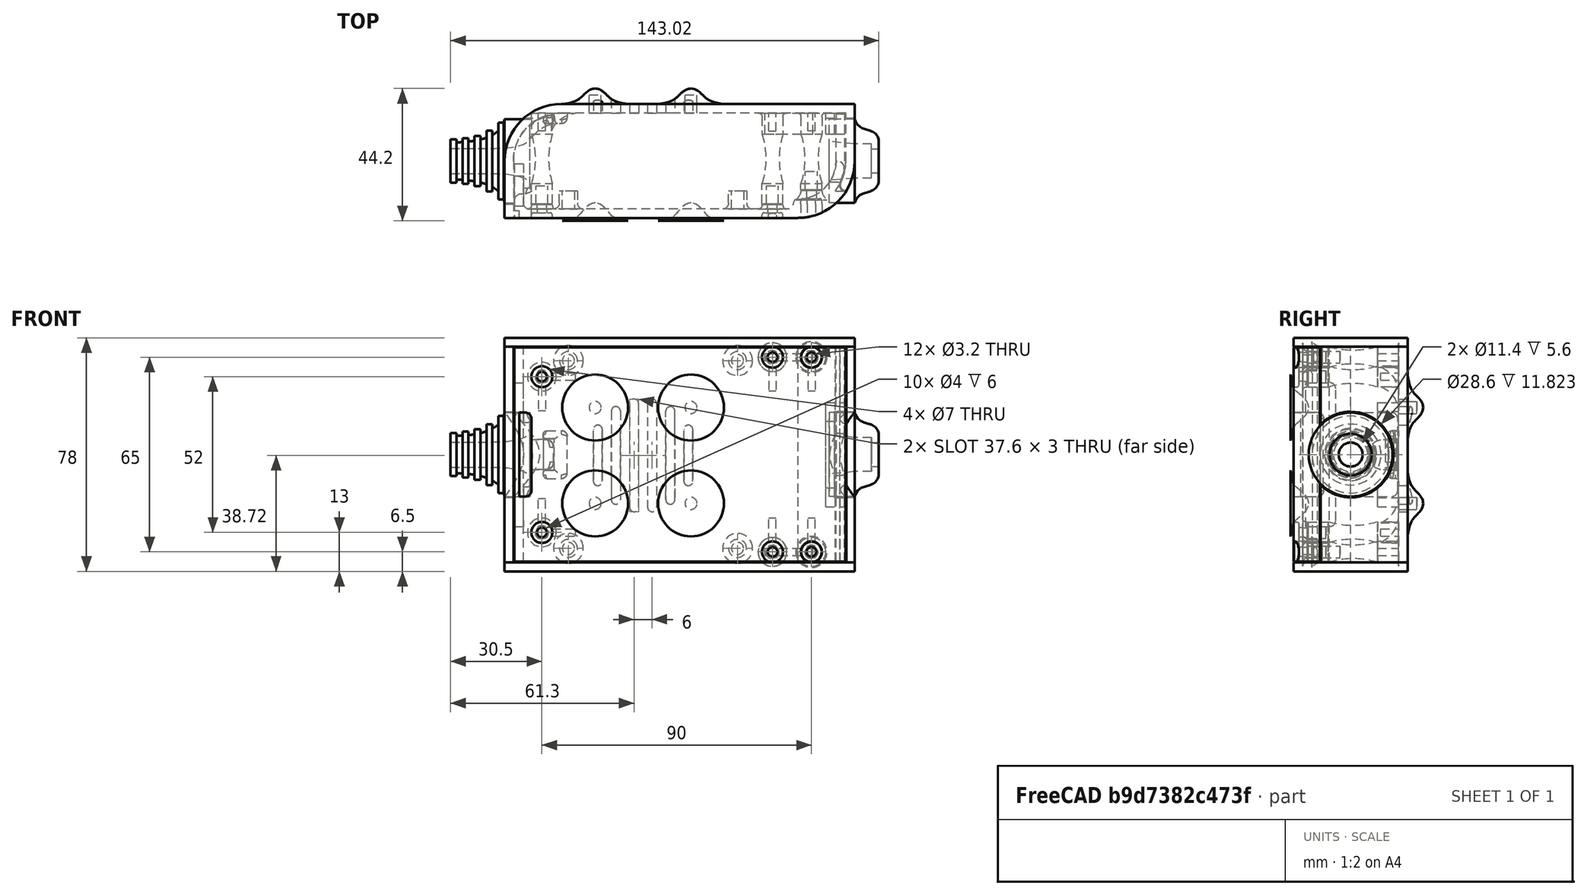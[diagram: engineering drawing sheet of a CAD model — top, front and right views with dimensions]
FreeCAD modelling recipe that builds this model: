
FCSTD DOCUMENT  (FreeCAD 0.19R0.19.2)
Label: enclosure_098
License: All rights reserved
LicenseURL: http://en.wikipedia.org/wiki/All_rights_reserved
objects: Part::Feature×72, Part::Revolution×72, Part::MultiFuse×53, Sketcher::SketchObject×30, Part::Fillet×22, Part::Cylinder×22, Part::Cut×20, Part::Extrusion×19, Part::Box×12, App::MeasureDistance×4
note: 322 computed .brp shape members not serialized (recipe doc carries the construction recipe); baked Part::Feature solids carry a one-line shape summary decoded from their .brp

FEATURE [Sketcher::SketchObject] Sketch  label="topSketch"
  FullyConstrained = true
  sketch-geometry (13):
    g0: LineSegment StartX=117 StartY=19 StartZ=0 EndX=117 EndY=38 EndZ=0
    g1: ArcOfCircle CenterX=98 CenterY=19 CenterZ=0 NormalX=0 NormalY=0 NormalZ=1 AngleXU=0 Radius=19 StartAngle=5.7297 EndAngle=6.28319
    g2: LineSegment StartX=0 StartY=3 StartZ=0 EndX=0 EndY=19 EndZ=0
    g3: LineSegment StartX=19 StartY=38 StartZ=0 EndX=117 EndY=38 EndZ=0
    g4: ArcOfCircle CenterX=19 CenterY=19 CenterZ=0 NormalX=0 NormalY=0 NormalZ=1 AngleXU=0 Radius=19 StartAngle=1.5708 EndAngle=3.14159
    g5: ArcOfCircle CenterX=19 CenterY=19 CenterZ=0 NormalX=0 NormalY=0 NormalZ=1 AngleXU=0 Radius=16 StartAngle=1.5708 EndAngle=3.14159
    g6: ArcOfCircle CenterX=98 CenterY=19 CenterZ=0 NormalX=0 NormalY=0 NormalZ=1 AngleXU=0 Radius=16 StartAngle=5.60905 EndAngle=6.28319
    g7: LineSegment StartX=114 StartY=19 StartZ=0 EndX=114 EndY=35 EndZ=0
    g8: LineSegment StartX=110.5 StartY=9.01251 StartZ=0 EndX=114.163 EndY=9.01251 EndZ=0
    g9: LineSegment StartX=114 StartY=35 StartZ=0 EndX=19 EndY=35 EndZ=0
    g10: LineSegment StartX=0 StartY=3 StartZ=0 EndX=0 EndY=0 EndZ=0
    g11: LineSegment StartX=3 StartY=0 StartZ=0 EndX=0 EndY=0 EndZ=0
    g12: LineSegment StartX=3 StartY=19 StartZ=0 EndX=3 EndY=0 EndZ=0
  constraints (33):
    c: Vertical(g0)
    c: Distance(g0) = 19
    c: Block(g0)
    c: Coincident(g1,g0)
    c: Block(g1)
    c: Vertical(g2)
    c: Block(g2)
    c: Coincident(g3,g0)
    c: Horizontal(g3)
    c: Distance(g3) = 98
    c: Coincident(g4,g3)
    c: Coincident(g4,g2)
    c: Block(g4)
    c: Coincident(g5,g4)
    c: Coincident(g6,g1)
    c: Block(g6)
    c: Block(g5)
    c: Coincident(g7,g6)
    c: Vertical(g7)
    c: Coincident(g8,g6)
    c: Coincident(g8,g1)
    c: Coincident(g9,g7)
    c: Coincident(g9,g5)
    c: Horizontal(g9)
    c: Tangent(g9,g5)
    c: Coincident(g10,g2)
    c: Distance(g10) = 3
    c: Vertical(g10)
    c: Coincident(g11,g10)
    c: Horizontal(g11)
    c: Coincident(g12,g5)
    c: Coincident(g12,g11)
    c: Vertical(g12)
FEATURE [Sketcher::SketchObject] Sketch001  label="bottomSketch"
  FullyConstrained = true
  sketch-geometry (32):
    g0: LineSegment StartX=3.3 StartY=-6.03275e-07 StartZ=0 EndX=98 EndY=-6.03275e-07 EndZ=0
    g1: ArcOfCircle CenterX=98 CenterY=19 CenterZ=0 NormalX=0 NormalY=0 NormalZ=1 AngleXU=0 Radius=19 StartAngle=4.71239 EndAngle=5.71103
    g2: LineSegment StartX=6.3 StartY=8 StartZ=0 EndX=3.3 EndY=8 EndZ=0
    g3: LineSegment StartX=3.3 StartY=8 StartZ=0 EndX=3.3 EndY=-6.03275e-07 EndZ=0
    g4: ArcOfCircle CenterX=8.3 CenterY=5 CenterZ=0 NormalX=0 NormalY=0 NormalZ=1 AngleXU=0 Radius=2 StartAngle=3.14159 EndAngle=4.71239
    g5: LineSegment StartX=6.3 StartY=8 StartZ=0 EndX=6.3 EndY=5 EndZ=0
    g6: ArcOfCircle CenterX=98 CenterY=19 CenterZ=0 NormalX=0 NormalY=0 NormalZ=1 AngleXU=0 Radius=12.7 StartAngle=4.71239 EndAngle=6.28319
    g7: LineSegment StartX=94.7 StartY=3 StartZ=0 EndX=8.3 EndY=3 EndZ=0
    g8-g12: Circle x5 (B-spline internal-alignment scaffolding for g13; pole/knot coordinates omitted)
    g13: BSplineCurve PolesCount=5 KnotsCount=3 Degree=3 IsPeriodic=0
    g14: GeomPoint X=98 Y=6.3 Z=0
    g15: GeomPoint X=96.3938 Y=4.71946 Z=0
    g16: GeomPoint X=94.7 Y=3 Z=0
    g17-g23: Circle x7 (B-spline internal-alignment scaffolding for g24; pole/knot coordinates omitted)
    g24: BSplineCurve PolesCount=7 KnotsCount=5 Degree=3 IsPeriodic=0
    g25-g29: GeomPoint x5 (B-spline internal-alignment scaffolding for g24; pole/knot coordinates omitted)
    g30: ArcOfCircle CenterX=98 CenterY=19 CenterZ=0 NormalX=0 NormalY=0 NormalZ=1 AngleXU=0 Radius=15.7 StartAngle=5.81226 EndAngle=6.28319
    g31: LineSegment StartX=110.7 StartY=19 StartZ=0 EndX=113.7 EndY=19 EndZ=0
  constraints (41):
    c: Horizontal(g0)
    c: Coincident(g1,g0)
    c: Block(g1)
    c: Horizontal(g2)
    c: Distance(g2) = 3
    c: Coincident(g3,g2)
    c: Vertical(g3)
    c: Coincident(g3,g0)
    c: Block(g4)
    c: Block(g2)
    c: Coincident(g5,g2)
    c: Coincident(g5,g4)
    c: Vertical(g5)
    c: Coincident(g6,g1)
    c: Block(g6)
    c: Coincident(g7,g4)
    c: Horizontal(g7)
    c: Block(g0)
    c: Block(g7)
    c: Block(g3)
    c: Coincident(g13,g6)
    c: Weight(g8) = 1
    c: Equal(g8, g9-g12) x4
    c: Coincident(g13,g7)
    c: InternalAlignment(g8-g12 -> g13) x5
    c: InternalAlignment(g14,g13)
    c: InternalAlignment(g15,g13)
    c: InternalAlignment(g16,g13)
    c: Block(g13)
    c: Weight(g17) = 1
    c: Equal(g17, g18-g23) x6
    c: Coincident(g24,g1)
    c: InternalAlignment(g17-g23 -> g24) x7
    c: InternalAlignment(g25-g29 -> g24) x5
    c: Block(g24)
    c: Coincident(g30,g24)
    c: Coincident(g31,g6)
    c: Coincident(g31,g30)
    c: Horizontal(g31)
    c: Block(g31)
    c: Block(g30)
FEATURE [Part::Extrusion] Extrude  label="top"
  Base = -> Sketch
  Dir = (0,0,1)
  DirMode = 2
  FaceMakerClass = Part::FaceMakerBullseye
  LengthFwd = 72
  LengthRev = 0
  Solid = true
  Symmetric = false
FEATURE [Part::Extrusion] Extrude001  label="bottom"
  Base = -> Sketch001
  Dir = (0,0,1)
  DirMode = 2
  FaceMakerClass = Part::FaceMakerBullseye
  LengthFwd = 71.4
  LengthRev = 0
  Placement = pos=(0,0,0.3) rot=(0,0,1;0rad)
  Solid = true
  Symmetric = false
FEATURE [Sketcher::SketchObject] Sketch002  label="topSketch001"
  FullyConstrained = true
  sketch-geometry (6):
    g0: LineSegment StartX=19 StartY=38 StartZ=0 EndX=117 EndY=38 EndZ=0
    g1: ArcOfCircle CenterX=19 CenterY=19 CenterZ=0 NormalX=0 NormalY=0 NormalZ=1 AngleXU=0 Radius=19 StartAngle=1.5708 EndAngle=3.14159
    g2: LineSegment StartX=117 StartY=38 StartZ=0 EndX=117 EndY=19 EndZ=0
    g3: LineSegment StartX=98 StartY=1.0161e-12 StartZ=0 EndX=5.22862e-06 EndY=1.0161e-12 EndZ=0
    g4: LineSegment StartX=5.22862e-06 StartY=19 StartZ=0 EndX=5.22862e-06 EndY=1.0161e-12 EndZ=0
    g5: ArcOfCircle CenterX=98 CenterY=19 CenterZ=0 NormalX=0 NormalY=0 NormalZ=1 AngleXU=0 Radius=19 StartAngle=4.71239 EndAngle=6.28319
  constraints (16):
    c: Horizontal(g0)
    c: Distance(g0) = 98
    c: Coincident(g1,g0)
    c: Block(g1)
    c: Coincident(g2,g0)
    c: Vertical(g2)
    c: Distance(g2) = 19
    c: Horizontal(g3)
    c: Coincident(g4,g1)
    c: Vertical(g4)
    c: Coincident(g3,g4)
    c: Block(g3)
    c: Coincident(g5,g2)
    c: Coincident(g5,g3)
    c: Block(g0)
    c: Block(g5)
FEATURE [Part::Extrusion] Extrude002  label="sideA"
  Base = -> Sketch002
  Dir = (0,0,1)
  DirMode = 2
  FaceMakerClass = Part::FaceMakerBullseye
  LengthFwd = 3
  LengthRev = 0
  Placement = pos=(0,0,-3) rot=(0,0,1;0rad)
  Solid = true
  Symmetric = false
FEATURE [Sketcher::SketchObject] Sketch003  label="topSketch002"
  FullyConstrained = true
  sketch-geometry (6):
    g0: LineSegment StartX=19 StartY=38 StartZ=0 EndX=117 EndY=38 EndZ=0
    g1: ArcOfCircle CenterX=19 CenterY=19 CenterZ=0 NormalX=0 NormalY=0 NormalZ=1 AngleXU=0 Radius=19 StartAngle=1.5708 EndAngle=3.14159
    g2: LineSegment StartX=117 StartY=38 StartZ=0 EndX=117 EndY=19 EndZ=0
    g3: LineSegment StartX=98 StartY=1.0161e-12 StartZ=0 EndX=5.22862e-06 EndY=1.0161e-12 EndZ=0
    g4: LineSegment StartX=5.22862e-06 StartY=19 StartZ=0 EndX=5.22862e-06 EndY=1.0161e-12 EndZ=0
    g5: ArcOfCircle CenterX=98 CenterY=19 CenterZ=0 NormalX=0 NormalY=0 NormalZ=1 AngleXU=0 Radius=19 StartAngle=4.71239 EndAngle=6.28319
  constraints (16):
    c: Horizontal(g0)
    c: Distance(g0) = 98
    c: Coincident(g1,g0)
    c: Block(g1)
    c: Coincident(g2,g0)
    c: Vertical(g2)
    c: Distance(g2) = 19
    c: Horizontal(g3)
    c: Coincident(g4,g1)
    c: Vertical(g4)
    c: Coincident(g3,g4)
    c: Block(g3)
    c: Coincident(g5,g2)
    c: Coincident(g5,g3)
    c: Block(g0)
    c: Block(g5)
FEATURE [Part::Extrusion] Extrude003  label="sideB"
  Base = -> Sketch003
  Dir = (0,0,1)
  DirMode = 2
  FaceMakerClass = Part::FaceMakerBullseye
  LengthFwd = 3
  LengthRev = 0
  Placement = pos=(0,0,72) rot=(0,0,1;0rad)
  Solid = true
  Symmetric = false
FEATURE [Sketcher::SketchObject] Sketch004
  FullyConstrained = true
  MapMode = 3
  Placement = pos=(0,0,0) rot=(1,0,0;1.5708rad)
  Support = -> [Extrude]
  sketch-geometry (8):
    g0: Circle CenterX=80.351 CenterY=-67.6202 CenterZ=0 NormalX=0 NormalY=0 NormalZ=1 AngleXU=0 Radius=2
    g1: Circle CenterX=80.351 CenterY=-67.6202 CenterZ=0 NormalX=0 NormalY=0 NormalZ=1 AngleXU=0 Radius=3
    g2: Circle CenterX=80.351 CenterY=-4.92017 CenterZ=0 NormalX=0 NormalY=0 NormalZ=1 AngleXU=0 Radius=2
    g3: Circle CenterX=80.351 CenterY=-4.92017 CenterZ=0 NormalX=0 NormalY=0 NormalZ=1 AngleXU=0 Radius=3
    g4: Circle CenterX=23.851 CenterY=-4.92017 CenterZ=0 NormalX=0 NormalY=0 NormalZ=1 AngleXU=0 Radius=2
    g5: Circle CenterX=23.851 CenterY=-4.92017 CenterZ=0 NormalX=0 NormalY=0 NormalZ=1 AngleXU=0 Radius=3
    g6: Circle CenterX=23.851 CenterY=-67.6202 CenterZ=0 NormalX=0 NormalY=0 NormalZ=1 AngleXU=0 Radius=2
    g7: Circle CenterX=23.851 CenterY=-67.6202 CenterZ=0 NormalX=0 NormalY=0 NormalZ=1 AngleXU=0 Radius=3
  constraints (8):
    c: Block(g3)
    c: Block(g2)
    c: Block(g1)
    c: Block(g0)
    c: Block(g6)
    c: Block(g7)
    c: Block(g4)
    c: Block(g5)
FEATURE [Part::Extrusion] Extrude004
  Base = -> Sketch004
  Dir = (0,-1,2e-16)
  DirMode = 2
  FaceMakerClass = Part::FaceMakerBullseye
  LengthFwd = 6
  LengthRev = 0
  Placement = pos=(0,9,0) rot=(0,0,1;0rad)
  Solid = true
  Symmetric = false
FEATURE [Sketcher::SketchObject] Sketch005
  FullyConstrained = true
  MapMode = 3
  Placement = pos=(0,0,0) rot=(1,0,0;1.5708rad)
  Support = -> [Extrude]
  sketch-geometry (8):
    g0: Circle CenterX=80.351 CenterY=-67.6202 CenterZ=0 NormalX=0 NormalY=0 NormalZ=1 AngleXU=0 Radius=3
    g1: Circle CenterX=80.351 CenterY=-4.92017 CenterZ=0 NormalX=0 NormalY=0 NormalZ=1 AngleXU=0 Radius=3
    g2: Circle CenterX=23.851 CenterY=-4.92017 CenterZ=0 NormalX=0 NormalY=0 NormalZ=1 AngleXU=0 Radius=3
    g3: Circle CenterX=23.851 CenterY=-67.6202 CenterZ=0 NormalX=0 NormalY=0 NormalZ=1 AngleXU=0 Radius=3
    g4: Circle CenterX=23.851 CenterY=-67.6202 CenterZ=0 NormalX=0 NormalY=0 NormalZ=1 AngleXU=0 Radius=5
    g5: Circle CenterX=80.351 CenterY=-67.6202 CenterZ=0 NormalX=0 NormalY=0 NormalZ=1 AngleXU=0 Radius=5
    g6: Circle CenterX=23.851 CenterY=-4.92017 CenterZ=0 NormalX=0 NormalY=0 NormalZ=1 AngleXU=0 Radius=5
    g7: Circle CenterX=80.351 CenterY=-4.92017 CenterZ=0 NormalX=0 NormalY=0 NormalZ=1 AngleXU=0 Radius=5
  constraints (8):
    c: Block(g1)
    c: Block(g0)
    c: Block(g3)
    c: Block(g2)
    c: Block(g5)
    c: Block(g4)
    c: Block(g6)
    c: Block(g7)
FEATURE [Part::Extrusion] Extrude005
  Base = -> Sketch005
  Dir = (0,-1,2e-16)
  DirMode = 2
  FaceMakerClass = Part::FaceMakerBullseye
  LengthFwd = 2
  LengthRev = 0
  Solid = true
  Symmetric = false
FEATURE [Sketcher::SketchObject] Sketch006
  FullyConstrained = true
  MapMode = 3
  Placement = pos=(0,0,0) rot=(1,0,0;1.5708rad)
  sketch-geometry (8):
    g0: Circle CenterX=80.351 CenterY=-67.6202 CenterZ=0 NormalX=0 NormalY=0 NormalZ=1 AngleXU=0 Radius=3
    g1: Circle CenterX=80.351 CenterY=-4.92017 CenterZ=0 NormalX=0 NormalY=0 NormalZ=1 AngleXU=0 Radius=3
    g2: Circle CenterX=23.851 CenterY=-4.92017 CenterZ=0 NormalX=0 NormalY=0 NormalZ=1 AngleXU=0 Radius=3
    g3: Circle CenterX=23.851 CenterY=-67.6202 CenterZ=0 NormalX=0 NormalY=0 NormalZ=1 AngleXU=0 Radius=3
    g4: Circle CenterX=23.851 CenterY=-67.6202 CenterZ=0 NormalX=0 NormalY=0 NormalZ=1 AngleXU=0 Radius=5
    g5: Circle CenterX=80.351 CenterY=-67.6202 CenterZ=0 NormalX=0 NormalY=0 NormalZ=1 AngleXU=0 Radius=5
    g6: Circle CenterX=23.851 CenterY=-4.92017 CenterZ=0 NormalX=0 NormalY=0 NormalZ=1 AngleXU=0 Radius=5
    g7: Circle CenterX=80.351 CenterY=-4.92017 CenterZ=0 NormalX=0 NormalY=0 NormalZ=1 AngleXU=0 Radius=5
  constraints (8):
    c: Block(g1)
    c: Block(g0)
    c: Block(g3)
    c: Block(g2)
    c: Block(g5)
    c: Block(g4)
    c: Block(g6)
    c: Block(g7)
FEATURE [Part::Extrusion] Extrude007
  Base = -> Sketch006
  Dir = (0,-1,2e-16)
  DirMode = 2
  FaceMakerClass = Part::FaceMakerBullseye
  LengthFwd = 2
  LengthRev = 0
  Solid = true
  Symmetric = false
FEATURE [Part::Fillet] Fillet
  Base = -> Extrude007
  Edges = 4 edges r=1.99: [Edge6,Edge12,Edge18,Edge24]
FEATURE [Part::Cut] Cut
  Base = -> Extrude005
  Placement = pos=(0,5,0) rot=(0,0,1;0rad)
  Tool = -> Fillet
FEATURE [Part::MultiFuse] Fusion  label="pCBScrews"
  Placement = pos=(-2.5,0,72.3) rot=(0,0,1;0rad)
  Shapes = -> [Extrude004,Cut]
FEATURE [App::MeasureDistance] Distance  label="Distance: 0.69 mm"
  Distance = 0.685967
  P1 = (24.0138,2.9647,0.3)
  P2 = (23.8901,3,-0.373787)
FEATURE [App::MeasureDistance] Distance001  label="Distance: 0.53 mm"
  Distance = 0.533607
  P1 = (80.2939,3,72.2334)
  P2 = (80.281,2.99661,71.7)
FEATURE [Part::Fillet] Fillet001
  Base = -> Extrude001
  Edges = 1 edges r=2.4: [Edge17]
FEATURE [Part::Fillet] Fillet002  label="bottom001"
  Base = -> Fillet001
  Edges = 1 edges r=2.4: [Edge36]
FEATURE [Part::Fillet] Fillet003  label="top001"
  Base = -> Extrude
  Edges = 1 edges r=2: [Edge1]
FEATURE [Sketcher::SketchObject] Sketch007
  FullyConstrained = true
  sketch-geometry (16):
    g0: LineSegment StartX=4 StartY=0 StartZ=0 EndX=4 EndY=2.4 EndZ=0
    g1: LineSegment StartX=4 StartY=2.4 StartZ=0 EndX=7 EndY=2.4 EndZ=0
    g2: LineSegment StartX=4 StartY=0 StartZ=0 EndX=5.7 EndY=0 EndZ=0
    g3: LineSegment StartX=5.7 StartY=0 StartZ=0 EndX=5.7 EndY=-5.6 EndZ=0
    g4-g8: Circle x5 (B-spline internal-alignment scaffolding for g9; pole/knot coordinates omitted)
    g9: BSplineCurve PolesCount=5 KnotsCount=3 Degree=3 IsPeriodic=0
    g10: GeomPoint X=7 Y=2.4 Z=0
    g11: GeomPoint X=10.4582 Y=-1.55472 Z=0
    g12: GeomPoint X=14 Y=-5.6 Z=0
    g13: LineSegment StartX=14 StartY=-5.6 StartZ=0 EndX=14 EndY=-14.1 EndZ=0
    g14: LineSegment StartX=14 StartY=-14.1 StartZ=0 EndX=6.5 EndY=-14.1 EndZ=0
    g15: LineSegment StartX=5.7 StartY=-5.6 StartZ=0 EndX=6.5 EndY=-14.1 EndZ=0
  constraints (28):
    c: Distance(g0) = 2.4
    c: Vertical(g0)
    c: Block(g0)
    c: Coincident(g1,g0)
    c: Horizontal(g1)
    c: Distance(g1) = 3
    c: Coincident(g2,g0)
    c: Horizontal(g2)
    c: Distance(g2) = 1.7
    c: Coincident(g3,g2)
    c: Vertical(g3)
    c: Distance(g3) = 5.6
    c: Coincident(g9,g1)
    c: Weight(g4) = 1
    c: Equal(g4, g5-g8) x4
    c: InternalAlignment(g4-g8 -> g9) x5
    c: InternalAlignment(g10,g9)
    c: InternalAlignment(g11,g9)
    c: InternalAlignment(g12,g9)
    c: Block(g9)
    c: Coincident(g13,g9)
    c: Vertical(g13)
    c: Distance(g13) = 8.5
    c: Coincident(g14,g13)
    c: Horizontal(g14)
    c: Distance(g14) = 7.5
    c: Coincident(g15,g3)
    c: Coincident(g15,g14)
FEATURE [Part::Feature] Face
  shape: bbox 10 x 16.5 x 2e-07 mm, 1 faces, 0 solids (baked)
FEATURE [Part::Revolution] Revolve  label="plugHousing"
  Angle = 360
  Axis = (0,1,0)
  Base = (0,0,0)
  FaceMakerClass = Part::FaceMakerBullseye
  Placement = pos=(0,0,36.15) rot=(0,0,1;0rad)
  Solid = false
  Source = -> Face
  Symmetric = false
FEATURE [Part::Feature] Face001
  shape: bbox 10 x 16.5 x 2e-07 mm, 1 faces, 0 solids (baked)
FEATURE [Part::Revolution] Revolve001  label="plugHousing001"
  Angle = 360
  Axis = (0,1,0)
  Base = (0,0,0)
  FaceMakerClass = Part::FaceMakerBullseye
  Placement = pos=(0,0,36.15) rot=(0,0,1;0rad)
  Solid = false
  Source = -> Face001
  Symmetric = false
FEATURE [Part::MultiFuse] Fusion001  label="plugHousing002"
  Placement = pos=(0,0,0) rot=(0,0,1;1.5708rad)
  Shapes = -> [Revolve001,Revolve]
FEATURE [Part::Feature] Face002
  shape: bbox 10 x 16.5 x 2e-07 mm, 1 faces, 0 solids (baked)
FEATURE [Part::Revolution] Revolve003  label="plugHousing005"
  Angle = 360
  Axis = (0,1,0)
  Base = (0,0,0)
  FaceMakerClass = Part::FaceMakerBullseye
  Placement = pos=(0,0,36.15) rot=(0,0,1;0rad)
  Solid = false
  Source = -> Face002
  Symmetric = false
FEATURE [Part::Feature] Face003
  shape: bbox 10 x 16.5 x 2e-07 mm, 1 faces, 0 solids (baked)
FEATURE [Part::Revolution] Revolve002  label="plugHousing003"
  Angle = 360
  Axis = (0,1,0)
  Base = (0,0,0)
  FaceMakerClass = Part::FaceMakerBullseye
  Placement = pos=(0,0,36.15) rot=(0,0,1;0rad)
  Solid = false
  Source = -> Face003
  Symmetric = false
FEATURE [Part::MultiFuse] Fusion002  label="plugHousing004"
  Placement = pos=(0,0,0) rot=(0,0,1;1.5708rad)
  Shapes = -> [Revolve002,Revolve003]
FEATURE [Part::MultiFuse] Fusion003  label="plugHousing006"
  Placement = pos=(0,19,0) rot=(0,0,1;3.14159rad)
  Shapes = -> [Fusion002,Fusion001]
FEATURE [Part::Feature] Face004
  shape: bbox 10 x 16.5 x 2e-07 mm, 1 faces, 0 solids (baked)
FEATURE [Part::Revolution] Revolve006  label="plugHousing010"
  Angle = 360
  Axis = (0,1,0)
  Base = (0,0,0)
  FaceMakerClass = Part::FaceMakerBullseye
  Placement = pos=(0,0,36.15) rot=(0,0,1;0rad)
  Solid = false
  Source = -> Face004
  Symmetric = false
FEATURE [Part::Feature] Face005
  shape: bbox 10 x 16.5 x 2e-07 mm, 1 faces, 0 solids (baked)
FEATURE [Part::Revolution] Revolve007  label="plugHousing011"
  Angle = 360
  Axis = (0,1,0)
  Base = (0,0,0)
  FaceMakerClass = Part::FaceMakerBullseye
  Placement = pos=(0,0,36.15) rot=(0,0,1;0rad)
  Solid = false
  Source = -> Face005
  Symmetric = false
FEATURE [Part::Feature] Face006
  shape: bbox 10 x 16.5 x 2e-07 mm, 1 faces, 0 solids (baked)
FEATURE [Part::Revolution] Revolve004  label="plugHousing007"
  Angle = 360
  Axis = (0,1,0)
  Base = (0,0,0)
  FaceMakerClass = Part::FaceMakerBullseye
  Placement = pos=(0,0,36.15) rot=(0,0,1;0rad)
  Solid = false
  Source = -> Face006
  Symmetric = false
FEATURE [Part::MultiFuse] Fusion004  label="plugHousing009"
  Placement = pos=(0,0,0) rot=(0,0,1;1.5708rad)
  Shapes = -> [Revolve004,Revolve007]
FEATURE [Part::Feature] Face007
  shape: bbox 10 x 16.5 x 2e-07 mm, 1 faces, 0 solids (baked)
FEATURE [Part::Revolution] Revolve005  label="plugHousing008"
  Angle = 360
  Axis = (0,1,0)
  Base = (0,0,0)
  FaceMakerClass = Part::FaceMakerBullseye
  Placement = pos=(0,0,36.15) rot=(0,0,1;0rad)
  Solid = false
  Source = -> Face007
  Symmetric = false
FEATURE [Part::MultiFuse] Fusion005  label="plugHousing012"
  Placement = pos=(0,0,0) rot=(0,0,1;1.5708rad)
  Shapes = -> [Revolve006,Revolve005]
FEATURE [Part::MultiFuse] Fusion006  label="plugHousing013"
  Placement = pos=(0,19,0) rot=(0,0,1;3.14159rad)
  Shapes = -> [Fusion005,Fusion004]
FEATURE [Part::MultiFuse] Fusion007  label="plugHousing014"
  Placement = pos=(122.621,0,-0.15) rot=(0,0,1;0rad)
  Shapes = -> [Fusion003,Fusion006]
FEATURE [Part::Cylinder] Cylinder002
  Angle = 360
  AttacherType = Attacher::AttachEngine3D
  Height = 20
  Placement = pos=(0,0,36.15) rot=(0,0,1;0rad)
  Radius = 4
FEATURE [Part::Cylinder] Cylinder003
  Angle = 360
  AttacherType = Attacher::AttachEngine3D
  Height = 10
  Placement = pos=(0,0,36.15) rot=(0,0,1;0rad)
  Radius = 4
FEATURE [Part::MultiFuse] Fusion009  label="removeToCreateHoleForPlugHousing"
  Placement = pos=(70,19,36.15) rot=(0,1,0;1.5708rad)
  Shapes = -> [Cylinder002,Cylinder003]
FEATURE [Part::Cylinder] Cylinder004
  Angle = 360
  AttacherType = Attacher::AttachEngine3D
  Height = 20
  Placement = pos=(0,0,36.15) rot=(0,0,1;0rad)
  Radius = 4
FEATURE [Part::Cylinder] Cylinder005
  Angle = 360
  AttacherType = Attacher::AttachEngine3D
  Height = 10
  Placement = pos=(0,0,36.15) rot=(0,0,1;0rad)
  Radius = 4
FEATURE [Part::MultiFuse] Fusion010  label="removeToCreateHoleForPlugHousing001"
  Placement = pos=(70,19,36.15) rot=(0,1,0;1.5708rad)
  Shapes = -> [Cylinder004,Cylinder005]
FEATURE [Part::Cut] Cut001
  Base = -> Fillet003
  Tool = -> Fusion010
FEATURE [Part::Cut] Cut002  label="Bottom"
  Base = -> Fillet002
  Tool = -> Fusion009
FEATURE [Part::Feature] Face008
  shape: bbox 10 x 16.5 x 2e-07 mm, 1 faces, 0 solids (baked)
FEATURE [Part::Revolution] Revolve011  label="plugHousing021"
  Angle = 360
  Axis = (0,1,0)
  Base = (0,0,0)
  FaceMakerClass = Part::FaceMakerBullseye
  Placement = pos=(0,0,36.15) rot=(0,0,1;0rad)
  Solid = false
  Source = -> Face008
  Symmetric = false
FEATURE [Part::Feature] Face009
  shape: bbox 10 x 16.5 x 2e-07 mm, 1 faces, 0 solids (baked)
FEATURE [Part::Revolution] Revolve012  label="plugHousing022"
  Angle = 360
  Axis = (0,1,0)
  Base = (0,0,0)
  FaceMakerClass = Part::FaceMakerBullseye
  Placement = pos=(0,0,36.15) rot=(0,0,1;0rad)
  Solid = false
  Source = -> Face009
  Symmetric = false
FEATURE [Part::Feature] Face010 .. Face013  x4 (patterned run collapsed; names and placements below)
  shape: bbox 10 x 16.5 x 2e-07 mm, 1 faces, 0 solids (baked)
FEATURE [Part::Revolution] Revolve015  label="plugHousing027"
  Angle = 360
  Axis = (0,1,0)
  Base = (0,0,0)
  FaceMakerClass = Part::FaceMakerBullseye
  Placement = pos=(0,0,36.15) rot=(0,0,1;0rad)
  Solid = false
  Source = -> Face013
  Symmetric = false
FEATURE [Part::Feature] Face014
  shape: bbox 10 x 16.5 x 2e-07 mm, 1 faces, 0 solids (baked)
FEATURE [Part::Feature] Face015
  shape: bbox 10 x 16.5 x 2e-07 mm, 1 faces, 0 solids (baked)
FEATURE [Part::Feature] Face016
  shape: bbox 10 x 16.5 x 2e-07 mm, 1 faces, 0 solids (baked)
FEATURE [Part::Revolution] Revolve019  label="plugHousing033"
  Angle = 360
  Axis = (0,1,0)
  Base = (0,0,0)
  FaceMakerClass = Part::FaceMakerBullseye
  Placement = pos=(0,0,36.15) rot=(0,0,1;0rad)
  Solid = false
  Source = -> Face016
  Symmetric = false
FEATURE [Part::Feature] Face017
  shape: bbox 10 x 16.5 x 2e-07 mm, 1 faces, 0 solids (baked)
FEATURE [Part::Revolution] Revolve020  label="plugHousing034"
  Angle = 360
  Axis = (0,1,0)
  Base = (0,0,0)
  FaceMakerClass = Part::FaceMakerBullseye
  Placement = pos=(0,0,36.15) rot=(0,0,1;0rad)
  Solid = false
  Source = -> Face017
  Symmetric = false
FEATURE [Part::Feature] Face018
  shape: bbox 10 x 16.5 x 2e-07 mm, 1 faces, 0 solids (baked)
FEATURE [Part::Revolution] Revolve016  label="plugHousing030"
  Angle = 360
  Axis = (0,1,0)
  Base = (0,0,0)
  FaceMakerClass = Part::FaceMakerBullseye
  Placement = pos=(0,0,36.15) rot=(0,0,1;0rad)
  Solid = false
  Source = -> Face018
  Symmetric = false
FEATURE [Part::MultiFuse] Fusion020  label="plugHousing038"
  Placement = pos=(0,0,0) rot=(0,0,1;1.5708rad)
  Shapes = -> [Revolve016,Revolve020]
FEATURE [Part::Feature] Face019
  shape: bbox 10 x 16.5 x 2e-07 mm, 1 faces, 0 solids (baked)
FEATURE [Part::Feature] Face020
  shape: bbox 10 x 16.5 x 2e-07 mm, 1 faces, 0 solids (baked)
FEATURE [Part::Revolution] Revolve017  label="plugHousing031"
  Angle = 360
  Axis = (0,1,0)
  Base = (0,0,0)
  FaceMakerClass = Part::FaceMakerBullseye
  Placement = pos=(0,0,36.15) rot=(0,0,1;0rad)
  Solid = false
  Source = -> Face020
  Symmetric = false
FEATURE [Part::MultiFuse] Fusion021  label="plugHousing039"
  Placement = pos=(0,0,0) rot=(0,0,1;1.5708rad)
  Shapes = -> [Revolve019,Revolve017]
FEATURE [Part::MultiFuse] Fusion023  label="plugHousing041"
  Placement = pos=(0,19,0) rot=(0,0,1;3.14159rad)
  Shapes = -> [Fusion021,Fusion020]
FEATURE [Part::Revolution] Revolve022  label="plugHousing043"
  Angle = 360
  Axis = (0,1,0)
  Base = (0,0,0)
  FaceMakerClass = Part::FaceMakerBullseye
  Placement = pos=(0,0,36.15) rot=(0,0,1;0rad)
  Solid = false
  Source = -> Face019
  Symmetric = false
FEATURE [Part::Feature] Face021
  shape: bbox 10 x 16.5 x 2e-07 mm, 1 faces, 0 solids (baked)
FEATURE [Part::Revolution] Revolve023  label="plugHousing044"
  Angle = 360
  Axis = (0,1,0)
  Base = (0,0,0)
  FaceMakerClass = Part::FaceMakerBullseye
  Placement = pos=(0,0,36.15) rot=(0,0,1;0rad)
  Solid = false
  Source = -> Face021
  Symmetric = false
FEATURE [Part::Feature] Face022
  shape: bbox 10 x 16.5 x 2e-07 mm, 1 faces, 0 solids (baked)
FEATURE [Part::Revolution] Revolve018  label="plugHousing032"
  Angle = 360
  Axis = (0,1,0)
  Base = (0,0,0)
  FaceMakerClass = Part::FaceMakerBullseye
  Placement = pos=(0,0,36.15) rot=(0,0,1;0rad)
  Solid = false
  Source = -> Face022
  Symmetric = false
FEATURE [Part::MultiFuse] Fusion022  label="plugHousing040"
  Placement = pos=(0,0,0) rot=(0,0,1;1.5708rad)
  Shapes = -> [Revolve018,Revolve023]
FEATURE [Part::Feature] Face023
  shape: bbox 10 x 16.5 x 2e-07 mm, 1 faces, 0 solids (baked)
FEATURE [Part::Revolution] Revolve021  label="plugHousing035"
  Angle = 360
  Axis = (0,1,0)
  Base = (0,0,0)
  FaceMakerClass = Part::FaceMakerBullseye
  Placement = pos=(0,0,36.15) rot=(0,0,1;0rad)
  Solid = false
  Source = -> Face023
  Symmetric = false
FEATURE [Part::MultiFuse] Fusion018  label="plugHousing036"
  Placement = pos=(0,0,0) rot=(0,0,1;1.5708rad)
  Shapes = -> [Revolve022,Revolve021]
FEATURE [Part::MultiFuse] Fusion019  label="plugHousing037"
  Placement = pos=(0,19,0) rot=(0,0,1;3.14159rad)
  Shapes = -> [Fusion018,Fusion022]
FEATURE [Part::MultiFuse] Fusion024  label="plugHousing042"
  Placement = pos=(122.621,0,-0.15) rot=(0,0,1;0rad)
  Shapes = -> [Fusion023,Fusion019]
FEATURE [Part::Cylinder] Cylinder006
  Angle = 360
  AttacherType = Attacher::AttachEngine3D
  Height = 20
  Placement = pos=(0,0,36.15) rot=(0,0,1;0rad)
  Radius = 14.3
FEATURE [Part::Cylinder] Cylinder007
  Angle = 360
  AttacherType = Attacher::AttachEngine3D
  Height = 10
  Placement = pos=(0,0,36.15) rot=(0,0,1;0rad)
  Radius = 4
FEATURE [Part::MultiFuse] Fusion026  label="removeToCreteHoleForPlugHousing"
  Placement = pos=(70,19,36) rot=(0,1,0;1.5708rad)
  Shapes = -> [Cylinder006,Cylinder007]
FEATURE [Part::Box] Box001  label="Cube001"
  AttacherType = Attacher::AttachEngine3D
  Height = 28
  Length = 3
  Placement = pos=(110.7,19,22) rot=(0,0,1;0rad)
  Width = 15.7
FEATURE [Part::Cut] Cut003  label="top002"
  Base = -> Cut001
  Tool = -> Fusion007
FEATURE [Part::Revolution] Revolve008  label="plugHousing015"
  Angle = 360
  Axis = (0,1,0)
  Base = (0,0,0)
  FaceMakerClass = Part::FaceMakerBullseye
  Placement = pos=(0,0,36.15) rot=(0,0,1;0rad)
  Solid = false
  Source = -> Face010
  Symmetric = false
FEATURE [Part::MultiFuse] Fusion013  label="plugHousing020"
  Placement = pos=(0,0,0) rot=(0,0,1;1.5708rad)
  Shapes = -> [Revolve008,Revolve012]
FEATURE [Part::Cut] Cut004  label="top003"
  Base = -> Cut003
  Placement = pos=(1,0,0) rot=(0,0,1;0rad)
  Tool = -> Fusion026
FEATURE [Part::Cylinder] Cylinder008
  Angle = 360
  AttacherType = Attacher::AttachEngine3D
  Height = 20
  Placement = pos=(0,0,36.15) rot=(0,0,1;0rad)
  Radius = 10.3
FEATURE [Part::Cylinder] Cylinder009
  Angle = 360
  AttacherType = Attacher::AttachEngine3D
  Height = 10
  Placement = pos=(0,0,36.15) rot=(0,0,1;0rad)
  Radius = 4
FEATURE [Part::MultiFuse] Fusion027  label="removeToCreteHoleForPlugHousing001"
  Placement = pos=(70,19,36) rot=(0,1,0;1.5708rad)
  Shapes = -> [Cylinder008,Cylinder009]
FEATURE [Part::Cut] Cut005  label="plugHousingTab"
  Base = -> Box001
  Tool = -> Fusion027
FEATURE [Part::MultiFuse] Fusion028  label="plugHousing045"
  Shapes = -> [Fusion024,Cut005]
FEATURE [Part::Box] Box002  label="Cube002"
  AttacherType = Attacher::AttachEngine3D
  Height = 28.8
  Length = 3
  Placement = pos=(107.3,28,21.6) rot=(0,0,1;0rad)
  Width = 7
FEATURE [Part::Box] Box003  label="Cube003"
  AttacherType = Attacher::AttachEngine3D
  Height = 3
  Length = 6.4
  Placement = pos=(107.3,28,18.6) rot=(0,0,1;0rad)
  Width = 7
FEATURE [Part::Box] Box004  label="Cube004"
  AttacherType = Attacher::AttachEngine3D
  Height = 3
  Length = 6.4
  Placement = pos=(107.3,28,50.4) rot=(0,0,1;0rad)
  Width = 7
FEATURE [Part::MultiFuse] Fusion029  label="plugHousingBracketHolder"
  Shapes = -> [Box004,Box002,Box003]
FEATURE [Part::Cylinder] Cylinder010
  Angle = 360
  AttacherType = Attacher::AttachEngine3D
  Height = 20
  Placement = pos=(0,0,36.15) rot=(0,0,1;0rad)
  Radius = 14.3
FEATURE [Part::Cylinder] Cylinder011
  Angle = 360
  AttacherType = Attacher::AttachEngine3D
  Height = 10
  Placement = pos=(0,0,36.15) rot=(0,0,1;0rad)
  Radius = 4
FEATURE [Part::MultiFuse] Fusion030  label="removeToCreteHoleForPlugHousing002"
  Placement = pos=(70,19,36) rot=(0,1,0;1.5708rad)
  Shapes = -> [Cylinder010,Cylinder011]
FEATURE [Part::Cut] Cut006  label="plugHousingBracketHolder001"
  Base = -> Fusion029
  Tool = -> Fusion030
FEATURE [Part::Cylinder] Cylinder012
  Angle = 360
  AttacherType = Attacher::AttachEngine3D
  Height = 20
  Placement = pos=(0,0,36.15) rot=(0,0,1;0rad)
  Radius = 7
FEATURE [Part::Cylinder] Cylinder013
  Angle = 360
  AttacherType = Attacher::AttachEngine3D
  Height = 10
  Placement = pos=(0,0,36.15) rot=(0,0,1;0rad)
  Radius = 4
FEATURE [Part::MultiFuse] Fusion032  label="removeToCreteHoleForPlugHousing003"
  Placement = pos=(70,19,36) rot=(0,1,0;1.5708rad)
  Shapes = -> [Cylinder012,Cylinder013]
FEATURE [Part::Cut] Cut007  label="bottom002"
  Base = -> Cut002
  Tool = -> Fusion032
FEATURE [Sketcher::SketchObject] Sketch008
  FullyConstrained = true
  sketch-geometry (54):
    g0: LineSegment StartX=-4.2 StartY=0 StartZ=0 EndX=-6.2 EndY=0 EndZ=0
    g1: LineSegment StartX=-14 StartY=-18 StartZ=0 EndX=-14 EndY=-26.5 EndZ=0
    g2: LineSegment StartX=-4.2 StartY=0 StartZ=0 EndX=-4.2 EndY=-13.4877 EndZ=0
    g3: Circle CenterX=-4.2 CenterY=-13.4877 CenterZ=0 NormalX=0 NormalY=0 NormalZ=1 AngleXU=0 Radius=1
    g4: Circle CenterX=-4.2 CenterY=-26.5 CenterZ=0 NormalX=0 NormalY=0 NormalZ=1 AngleXU=0 Radius=1
    g5: Circle CenterX=-8.2 CenterY=-26.5 CenterZ=0 NormalX=0 NormalY=0 NormalZ=1 AngleXU=0 Radius=1
    g6: BSplineCurve PolesCount=3 KnotsCount=2 Degree=2 IsPeriodic=0
    g7: GeomPoint X=-4.2 Y=-13.4877 Z=0
    g8: GeomPoint X=-8.2 Y=-26.5 Z=0
    g9: LineSegment StartX=-14 StartY=-26.5 StartZ=0 EndX=-8.2 EndY=-26.5 EndZ=0
    g10: LineSegment StartX=-10.15 StartY=-12 StartZ=0 EndX=-10.15 EndY=-14 EndZ=0
    g11: LineSegment StartX=-12.8401 StartY=-16 StartZ=0 EndX=-10.1571 EndY=-16 EndZ=0
    g12: LineSegment StartX=-10.15 StartY=-14 StartZ=0 EndX=-8.70761 EndY=-14 EndZ=0
    g13: LineSegment StartX=-12.8401 StartY=-16 StartZ=0 EndX=-12.8401 EndY=-17.6958 EndZ=0
    g14: LineSegment StartX=-10.15 StartY=-12 StartZ=0 EndX=-7.79258 EndY=-12 EndZ=0
    g15: Circle CenterX=-6.2215 CenterY=-2 CenterZ=0 NormalX=0 NormalY=0 NormalZ=1 AngleXU=0 Radius=1
    g16: Circle CenterX=-6.22762 CenterY=-2.58724 CenterZ=0 NormalX=0 NormalY=0 NormalZ=1 AngleXU=0 Radius=1
    g17: Circle CenterX=-6.32538 CenterY=-4 CenterZ=0 NormalX=0 NormalY=0 NormalZ=1 AngleXU=0 Radius=1
    g18: BSplineCurve PolesCount=3 KnotsCount=2 Degree=2 IsPeriodic=0
    g19: GeomPoint X=-6.2215 Y=-2 Z=0
    g20: GeomPoint X=-6.32538 Y=-4 Z=0
    g21: Circle CenterX=-6.48644 CenterY=-5.99526 CenterZ=0 NormalX=0 NormalY=0 NormalZ=1 AngleXU=0 Radius=1
    g22: Circle CenterX=-6.58486 CenterY=-6.99526 CenterZ=0 NormalX=0 NormalY=0 NormalZ=1 AngleXU=0 Radius=1
    g23: Circle CenterX=-6.77343 CenterY=-8 CenterZ=0 NormalX=0 NormalY=0 NormalZ=1 AngleXU=0 Radius=1
    g24: BSplineCurve PolesCount=3 KnotsCount=2 Degree=2 IsPeriodic=0
    g25: GeomPoint X=-6.48644 Y=-5.99526 Z=0
    g26: GeomPoint X=-6.77343 Y=-8 Z=0
    g27: Circle CenterX=-7.19003 CenterY=-10 CenterZ=0 NormalX=0 NormalY=0 NormalZ=1 AngleXU=0 Radius=1
    g28: Circle CenterX=-7.44407 CenterY=-11.0915 CenterZ=0 NormalX=0 NormalY=0 NormalZ=1 AngleXU=0 Radius=1
    g29: Circle CenterX=-7.79258 CenterY=-12 CenterZ=0 NormalX=0 NormalY=0 NormalZ=1 AngleXU=0 Radius=1
    g30: BSplineCurve PolesCount=3 KnotsCount=2 Degree=2 IsPeriodic=0
    g31: GeomPoint X=-7.19003 Y=-10 Z=0
    g32: GeomPoint X=-7.79258 Y=-12 Z=0
    g33: Circle CenterX=-8.70761 CenterY=-14 CenterZ=0 NormalX=0 NormalY=0 NormalZ=1 AngleXU=0 Radius=1
    g34: Circle CenterX=-9.33087 CenterY=-15.1837 CenterZ=0 NormalX=0 NormalY=0 NormalZ=1 AngleXU=0 Radius=1
    g35: Circle CenterX=-10.1571 CenterY=-16 CenterZ=0 NormalX=0 NormalY=0 NormalZ=1 AngleXU=0 Radius=1
    g36: BSplineCurve PolesCount=3 KnotsCount=2 Degree=2 IsPeriodic=0
    g37: GeomPoint X=-8.70761 Y=-14 Z=0
    g38: GeomPoint X=-10.1571 Y=-16 Z=0
    g39: Circle CenterX=-12.8401 CenterY=-17.6958 CenterZ=0 NormalX=0 NormalY=0 NormalZ=1 AngleXU=0 Radius=1
    g40: Circle CenterX=-13.3521 CenterY=-17.9027 CenterZ=0 NormalX=0 NormalY=0 NormalZ=1 AngleXU=0 Radius=1
    g41: Circle CenterX=-14 CenterY=-18 CenterZ=0 NormalX=0 NormalY=0 NormalZ=1 AngleXU=0 Radius=1
    g42: BSplineCurve PolesCount=3 KnotsCount=2 Degree=2 IsPeriodic=0
    g43: GeomPoint X=-12.8401 Y=-17.6958 Z=0
    g44: GeomPoint X=-14 Y=-18 Z=0
    g45: LineSegment StartX=-6.2 StartY=0 StartZ=0 EndX=-7.2 EndY=0 EndZ=0
    g46: LineSegment StartX=-7.2 StartY=0 StartZ=0 EndX=-7.2 EndY=-2 EndZ=0
    g47: LineSegment StartX=-7.2 StartY=-2 StartZ=0 EndX=-6.2215 EndY=-2 EndZ=0
    g48: LineSegment StartX=-6.32538 StartY=-4 StartZ=0 EndX=-7.65538 EndY=-4 EndZ=0
    g49: LineSegment StartX=-7.65538 StartY=-4 StartZ=0 EndX=-7.65538 EndY=-5.99526 EndZ=0
    g50: LineSegment StartX=-7.65538 StartY=-5.99526 StartZ=0 EndX=-6.48644 EndY=-5.99526 EndZ=0
    g51: LineSegment StartX=-6.77343 StartY=-8 StartZ=0 EndX=-8.43343 EndY=-8 EndZ=0
    g52: LineSegment StartX=-8.43343 StartY=-8 StartZ=0 EndX=-8.43343 EndY=-10 EndZ=0
    g53: LineSegment StartX=-8.43343 StartY=-10 StartZ=0 EndX=-7.19003 EndY=-10 EndZ=0
  constraints (112):
    c: Horizontal(g0)
    c: Distance(g0) = 2
    c: Block(g0)
    c: Vertical(g1)
    c: Coincident(g2,g0)
    c: Vertical(g2)
    c: Block(g2)
    c: Coincident(g6,g2)
    c: Weight(g3) = 1
    c: Equal(g3,g4)
    c: Equal(g3,g5)
    c: InternalAlignment(g3,g6)
    c: InternalAlignment(g4,g6)
    c: InternalAlignment(g5,g6)
    c: InternalAlignment(g7,g6)
    c: InternalAlignment(g8,g6)
    c: Block(g6)
    c: Coincident(g9,g1)
    c: Coincident(g9,g6)
    c: Horizontal(g9)
    c: Vertical(g10)
    c: Block(g10)
    c: Horizontal(g11)
    c: Block(g11)
    c: Coincident(g12,g10)
    c: Horizontal(g12)
    c: Block(g12)
    c: Coincident(g13,g11)
    c: Vertical(g13)
    c: Block(g13)
    c: Coincident(g14,g10)
    c: Horizontal(g14)
    c: Block(g14)
    c: Block(g9)
    c: Block(g1)
    c: Weight(g15) = 1
    c: Equal(g15,g16)
    c: Equal(g15,g17)
    c: InternalAlignment(g15,g18)
    c: InternalAlignment(g16,g18)
    c: InternalAlignment(g17,g18)
    c: InternalAlignment(g19,g18)
    c: InternalAlignment(g20,g18)
    c: Weight(g21) = 1
    c: Equal(g21,g22)
    c: Equal(g21,g23)
    c: InternalAlignment(g21,g24)
    c: InternalAlignment(g22,g24)
    c: InternalAlignment(g23,g24)
    c: InternalAlignment(g25,g24)
    c: InternalAlignment(g26,g24)
    c: Weight(g27) = 1
    c: Equal(g27,g28)
    c: Equal(g27,g29)
    c: Coincident(g30,g14)
    c: InternalAlignment(g27,g30)
    c: InternalAlignment(g28,g30)
    c: InternalAlignment(g29,g30)
    c: InternalAlignment(g31,g30)
    c: InternalAlignment(g32,g30)
    c: Coincident(g36,g12)
    c: Weight(g33) = 1
    c: Equal(g33,g34)
    c: Equal(g33,g35)
    c: Coincident(g36,g11)
    c: InternalAlignment(g33,g36)
    c: InternalAlignment(g34,g36)
    c: InternalAlignment(g35,g36)
    c: InternalAlignment(g37,g36)
    c: InternalAlignment(g38,g36)
    c: Coincident(g42,g13)
    c: Weight(g39) = 1
    c: Equal(g39,g40)
    c: Equal(g39,g41)
    c: Coincident(g42,g1)
    c: InternalAlignment(g39,g42)
    c: InternalAlignment(g40,g42)
    c: InternalAlignment(g41,g42)
    c: InternalAlignment(g43,g42)
    c: InternalAlignment(g44,g42)
    c: Block(g18)
    c: Block(g24)
    c: Block(g30)
    c: Block(g36)
    c: Block(g42)
    c: Horizontal(g45)
    c: Coincident(g45,g0)
    c: Vertical(g46)
    c: Coincident(g46,g45)
    c: Coincident(g47,g46)
    c: Coincident(g47,g18)
    c: Horizontal(g47)
    c: Block(g46)
    c: Coincident(g48,g18)
    c: Horizontal(g48)
    c: Distance(g48) = 1.33
    c: Vertical(g49)
    c: Coincident(g49,g48)
    c: Coincident(g50,g49)
    c: Coincident(g50,g24)
    c: Horizontal(g50)
    c: Tangent(g50,g22)
    c: Horizontal(g51)
    c: Coincident(g51,g24)
    c: Block(g51)
    c: Vertical(g52)
    c: Block(g52)
    c: Coincident(g52,g51)
    c: Coincident(g53,g52)
    c: Coincident(g53,g30)
    c: Horizontal(g53)
    c: Distance(g1) = 8.5
FEATURE [Part::Feature] Face024
  shape: bbox 9.8 x 26.5 x 2e-07 mm, 1 faces, 0 solids (baked)
FEATURE [Part::Revolution] Revolve024
  Angle = 360
  Axis = (0,1,0)
  Base = (0,0,0)
  FaceMakerClass = Part::FaceMakerBullseye
  Placement = pos=(0,0,0) rot=(0,0,1;1.5708rad)
  Solid = false
  Source = -> Face024
  Symmetric = false
FEATURE [Part::Feature] Face025
  shape: bbox 9.8 x 26.5 x 2e-07 mm, 1 faces, 0 solids (baked)
FEATURE [Part::Revolution] Revolve025
  Angle = 360
  Axis = (0,1,0)
  Base = (0,0,0)
  FaceMakerClass = Part::FaceMakerBullseye
  Placement = pos=(0,0,0) rot=(0,0,1;1.5708rad)
  Solid = false
  Source = -> Face025
  Symmetric = false
FEATURE [Part::MultiFuse] Fusion033
  Placement = pos=(-18,19,36) rot=(0,0,1;0rad)
  Shapes = -> [Revolve025,Revolve024]
FEATURE [Part::Cylinder] Cylinder014
  Angle = 360
  AttacherType = Attacher::AttachEngine3D
  Height = 20
  Placement = pos=(0,0,36.15) rot=(0,0,1;0rad)
  Radius = 14.3
FEATURE [Part::Cylinder] Cylinder015
  Angle = 360
  AttacherType = Attacher::AttachEngine3D
  Height = 10
  Placement = pos=(0,0,36.15) rot=(0,0,1;0rad)
  Radius = 4
FEATURE [Part::MultiFuse] Fusion034  label="removeToCreteHoleForPlugHousing004"
  Placement = pos=(-42,19,36) rot=(0,1,0;1.5708rad)
  Shapes = -> [Cylinder014,Cylinder015]
FEATURE [Part::Cut] Cut008  label="top004"
  Base = -> Cut004
  Placement = pos=(-1,0,0) rot=(0,0,1;0rad)
  Tool = -> Fusion034
FEATURE [Part::Box] Box005  label="Cube005"
  AttacherType = Attacher::AttachEngine3D
  Height = 28
  Length = 3
  Placement = pos=(110.7,19,22) rot=(0,0,1;0rad)
  Width = 15.7
FEATURE [Part::Cylinder] Cylinder016
  Angle = 360
  AttacherType = Attacher::AttachEngine3D
  Height = 10
  Placement = pos=(0,0,36.15) rot=(0,0,1;0rad)
  Radius = 4
FEATURE [Part::Cylinder] Cylinder017
  Angle = 360
  AttacherType = Attacher::AttachEngine3D
  Height = 20
  Placement = pos=(0,0,36.15) rot=(0,0,1;0rad)
  Radius = 10.3
FEATURE [Part::MultiFuse] Fusion035  label="removeToCreteHoleForPlugHousing005"
  Placement = pos=(70,19,36) rot=(0,1,0;1.5708rad)
  Shapes = -> [Cylinder017,Cylinder016]
FEATURE [Part::Cut] Cut009  label="plugHousingTab001"
  Base = -> Box005
  Placement = pos=(-107.4,-14,0) rot=(0,0,1;0rad)
  Tool = -> Fusion035
FEATURE [Part::Box] Box006  label="Cube006"
  AttacherType = Attacher::AttachEngine3D
  Height = 28
  Length = 3
  Placement = pos=(110.7,19,22) rot=(0,0,1;0rad)
  Width = 15.7
FEATURE [Part::Cylinder] Cylinder018
  Angle = 360
  AttacherType = Attacher::AttachEngine3D
  Height = 10
  Placement = pos=(0,0,36.15) rot=(0,0,1;0rad)
  Radius = 4
FEATURE [Part::Cylinder] Cylinder019
  Angle = 360
  AttacherType = Attacher::AttachEngine3D
  Height = 20
  Placement = pos=(0,0,36.15) rot=(0,0,1;0rad)
  Radius = 10.3
FEATURE [Part::MultiFuse] Fusion036  label="removeToCreteHoleForPlugHousing006"
  Placement = pos=(70,19,36) rot=(0,1,0;1.5708rad)
  Shapes = -> [Cylinder019,Cylinder018]
FEATURE [Part::Cut] Cut010  label="plugHousingTab002"
  Base = -> Box006
  Placement = pos=(-107.4,-14,0) rot=(0,0,1;0rad)
  Tool = -> Fusion036
FEATURE [Part::MultiFuse] Fusion037
  Placement = pos=(9.6,23,0) rot=(0,0,1;3.14159rad)
  Shapes = -> [Cut009,Cut010]
FEATURE [Part::Box] Box  label="Cube"
  AttacherType = Attacher::AttachEngine3D
  Height = 10
  Length = 3
  Placement = pos=(3.3,4,12) rot=(0,0,1;0rad)
  Width = 10
FEATURE [Part::Fillet] Fillet004
  Base = -> Fusion028
  Edges = 1 edges r=2: [Edge25]
FEATURE [Part::Fillet] Fillet005  label="plugHousing046"
  Base = -> Fillet004
  Edges = 1 edges r=2: [Edge8]
FEATURE [Part::Fillet] Fillet006
  Base = -> Box
  Edges = 1 edges r=2: [Edge11]
FEATURE [Part::Box] Box007  label="Cube007"
  AttacherType = Attacher::AttachEngine3D
  Height = 10
  Length = 3
  Placement = pos=(3.3,4,50) rot=(0,0,1;0rad)
  Width = 10
FEATURE [Part::Fillet] Fillet007
  Base = -> Box007
  Edges = 1 edges r=2: [Edge12]
FEATURE [Part::Box] Box008  label="Cube008"
  AttacherType = Attacher::AttachEngine3D
  Height = 28
  Length = 4
  Placement = pos=(5,0,22) rot=(0,0,1;0rad)
  Width = 10
FEATURE [Part::Fillet] Fillet008
  Base = -> Box008
  Edges = 1 edges r=1: [Edge7]
FEATURE [Part::Fillet] Fillet009
  Base = -> Fillet008
  Edges = 1 edges r=2: [Edge5]
FEATURE [Part::Fillet] Fillet010
  Base = -> Fillet009
  Edges = 1 edges r=2: [Edge2]
FEATURE [Sketcher::SketchObject] Sketch009  label="topSketch003"
  FullyConstrained = true
  sketch-geometry (4):
    g0: LineSegment StartX=16.8446 StartY=31.512 StartZ=0 EndX=16.3251 EndY=34.4666 EndZ=0
    g1: ArcOfCircle CenterX=19 CenterY=19.2524 CenterZ=0 NormalX=0 NormalY=0 NormalZ=1 AngleXU=0 Radius=15.4476 StartAngle=1.74483 EndAngle=2.72717
    g2: ArcOfCircle CenterX=19 CenterY=19.2524 CenterZ=0 NormalX=0 NormalY=0 NormalZ=1 AngleXU=0 Radius=12.4476 StartAngle=1.74483 EndAngle=2.73189
    g3: LineSegment StartX=4.86004 StartY=25.4725 StartZ=0 EndX=7.58253 EndY=24.2107 EndZ=0
  constraints (7):
    c: Block(g0)
    c: Coincident(g1,g0)
    c: Coincident(g2,g0)
    c: Coincident(g3,g1)
    c: Coincident(g3,g2)
    c: Block(g1)
    c: Block(g2)
FEATURE [Part::Extrusion] Extrude008
  Base = -> Sketch009
  Dir = (0,0,1)
  DirMode = 2
  FaceMakerClass = Part::FaceMakerBullseye
  LengthFwd = 10
  LengthRev = 0
  Placement = pos=(0,0,31) rot=(0,0,1;0rad)
  Solid = true
  Symmetric = false
FEATURE [Part::Cylinder] Cylinder020
  Angle = 360
  AttacherType = Attacher::AttachEngine3D
  Height = 20
  Placement = pos=(0,0,36.15) rot=(0,0,1;0rad)
  Radius = 8.2
FEATURE [Part::Cylinder] Cylinder021
  Angle = 360
  AttacherType = Attacher::AttachEngine3D
  Height = 10
  Placement = pos=(0,0,36.15) rot=(0,0,1;0rad)
  Radius = 4
FEATURE [Part::MultiFuse] Fusion038  label="removeToCreteHoleForPlugHousing007"
  Placement = pos=(-42,19,36) rot=(0,1,0;1.5708rad)
  Shapes = -> [Cylinder020,Cylinder021]
FEATURE [Part::Cut] Cut011
  Base = -> Extrude008
  Tool = -> Fusion038
FEATURE [Part::Fillet] Fillet011
  Base = -> Cut011
  Edges = 1 edges r=2: [Edge1]
FEATURE [Part::Fillet] Fillet012
  Base = -> Fillet011
  Edges = 1 edges r=2.5: [Edge1]
FEATURE [Part::Fillet] Fillet013
  Base = -> Fillet012
  Edges = 1 edges r=2.5: [Edge2]
FEATURE [Part::Box] Box010  label="Cube010"
  AttacherType = Attacher::AttachEngine3D
  Height = 16
  Length = 8
  Placement = pos=(12.7,31.52,28) rot=(0,0,1;0rad)
  Width = 4
FEATURE [Sketcher::SketchObject] Sketch010  label="topSketch004"
  FullyConstrained = true
  sketch-geometry (4):
    g0: LineSegment StartX=16.8446 StartY=31.512 StartZ=0 EndX=16.3251 EndY=34.4666 EndZ=0
    g1: ArcOfCircle CenterX=19 CenterY=19.2524 CenterZ=0 NormalX=0 NormalY=0 NormalZ=1 AngleXU=0 Radius=15.4476 StartAngle=1.74483 EndAngle=2.72717
    g2: ArcOfCircle CenterX=19 CenterY=19.2524 CenterZ=0 NormalX=0 NormalY=0 NormalZ=1 AngleXU=0 Radius=12.4476 StartAngle=1.74483 EndAngle=2.73189
    g3: LineSegment StartX=4.86004 StartY=25.4725 StartZ=0 EndX=7.58253 EndY=24.2107 EndZ=0
  constraints (7):
    c: Block(g0)
    c: Coincident(g1,g0)
    c: Coincident(g2,g0)
    c: Coincident(g3,g1)
    c: Coincident(g3,g2)
    c: Block(g1)
    c: Block(g2)
FEATURE [Part::Cylinder] Cylinder022
  Angle = 360
  AttacherType = Attacher::AttachEngine3D
  Height = 10
  Placement = pos=(0,0,36.15) rot=(0,0,1;0rad)
  Radius = 4
FEATURE [Sketcher::SketchObject] Sketch011  label="topSketch005"
  FullyConstrained = true
  sketch-geometry (4):
    g0: LineSegment StartX=16.8446 StartY=31.512 StartZ=0 EndX=16.3251 EndY=34.4666 EndZ=0
    g1: ArcOfCircle CenterX=19 CenterY=19.2524 CenterZ=0 NormalX=0 NormalY=0 NormalZ=1 AngleXU=0 Radius=15.4476 StartAngle=1.74483 EndAngle=2.72717
    g2: ArcOfCircle CenterX=19 CenterY=19.2524 CenterZ=0 NormalX=0 NormalY=0 NormalZ=1 AngleXU=0 Radius=12.4476 StartAngle=1.74483 EndAngle=2.73189
    g3: LineSegment StartX=4.86004 StartY=25.4725 StartZ=0 EndX=7.58253 EndY=24.2107 EndZ=0
  constraints (7):
    c: Block(g0)
    c: Coincident(g1,g0)
    c: Coincident(g2,g0)
    c: Coincident(g3,g1)
    c: Coincident(g3,g2)
    c: Block(g1)
    c: Block(g2)
FEATURE [Part::Extrusion] Extrude010
  Base = -> Sketch011
  Dir = (0,0,1)
  DirMode = 2
  FaceMakerClass = Part::FaceMakerBullseye
  LengthFwd = 10.6
  LengthRev = 0
  Placement = pos=(0,0,31) rot=(0,0,1;0rad)
  Solid = true
  Symmetric = false
FEATURE [Part::Cylinder] Cylinder023
  Angle = 360
  AttacherType = Attacher::AttachEngine3D
  Height = 20
  Placement = pos=(0,0,36.15) rot=(0,0,1;0rad)
  Radius = 8.2
FEATURE [Part::MultiFuse] Fusion039  label="removeToCreteHoleForPlugHousing008"
  Placement = pos=(-42,19,36) rot=(0,1,0;1.5708rad)
  Shapes = -> [Cylinder023,Cylinder022]
FEATURE [Part::Cut] Cut012
  Base = -> Extrude010
  Placement = pos=(0,0,-0.3) rot=(0,0,1;0rad)
  Tool = -> Fusion039
FEATURE [Part::Cut] Cut013
  Base = -> Box010
  Tool = -> Cut012
FEATURE [Part::Fillet] Fillet014
  Base = -> Cut013
  Edges = 1 edges r=0.7: [Edge13]
FEATURE [Part::Fillet] Fillet015
  Base = -> Fillet014
  Edges = 1 edges r=0.7: [Edge13]
FEATURE [Part::Fillet] Fillet016
  Base = -> Fillet015
  Edges = 1 edges r=0.7: [Edge16]
FEATURE [Part::Fillet] Fillet017
  Base = -> Fillet016
  Edges = 1 edges r=0.7: [Edge11]
FEATURE [Part::Fillet] Fillet018
  Base = -> Fillet017
  Edges = 1 edges r=0.7: [Edge10]
FEATURE [Part::Fillet] Fillet019
  Base = -> Fillet018
  Edges = 1 edges r=1.2: [Edge5]
FEATURE [Part::Fillet] Fillet020
  Base = -> Fillet019
  Edges = 1 edges r=1.2: [Edge12]
FEATURE [Part::Fillet] Fillet021
  Base = -> Fillet020
  Edges = 1 edges r=2: [Edge1]
  Placement = pos=(0.3,0,0) rot=(0,0,1;0rad)
FEATURE [Part::MultiFuse] Fusion040  label="top005"
  Shapes = -> [Cut008,Fillet021]
FEATURE [Part::MultiFuse] Fusion041  label="wireHolder"
  Shapes = -> [Fusion033,Fillet013]
FEATURE [Part::MultiFuse] Fusion042
  Shapes = -> [Fillet007,Fusion041]
FEATURE [Part::MultiFuse] Fusion043  label="wireHolder001"
  Shapes = -> [Fusion042,Fillet010]
FEATURE [Part::MultiFuse] Fusion044  label="wireHolder002"
  Shapes = -> [Fillet006,Fusion037,Fusion043]
FEATURE [Part::Feature] Face026
  shape: bbox 11 x 6 x 2e-07 mm, 1 faces, 0 solids (baked)
FEATURE [Part::Revolution] Revolve026
  Angle = 360
  Axis = (0,1,0)
  Base = (0,0,0)
  FaceMakerClass = Part::FaceMakerBullseye
  Placement = pos=(30.3,-1,19.7) rot=(0,0,1;0rad)
  Solid = false
  Source = -> Face026
  Symmetric = false
FEATURE [Sketcher::SketchObject] Sketch013  label="topSketch006"
  FullyConstrained = true
  sketch-geometry (13):
    g0: LineSegment StartX=117 StartY=19 StartZ=0 EndX=117 EndY=38 EndZ=0
    g1: ArcOfCircle CenterX=98 CenterY=19 CenterZ=0 NormalX=0 NormalY=0 NormalZ=1 AngleXU=0 Radius=19 StartAngle=5.7297 EndAngle=6.28319
    g2: LineSegment StartX=0 StartY=3 StartZ=0 EndX=0 EndY=19 EndZ=0
    g3: LineSegment StartX=19 StartY=38 StartZ=0 EndX=117 EndY=38 EndZ=0
    g4: ArcOfCircle CenterX=19 CenterY=19 CenterZ=0 NormalX=0 NormalY=0 NormalZ=1 AngleXU=0 Radius=19 StartAngle=1.5708 EndAngle=3.14159
    g5: ArcOfCircle CenterX=19 CenterY=19 CenterZ=0 NormalX=0 NormalY=0 NormalZ=1 AngleXU=0 Radius=16 StartAngle=1.5708 EndAngle=3.14159
    g6: ArcOfCircle CenterX=98 CenterY=19 CenterZ=0 NormalX=0 NormalY=0 NormalZ=1 AngleXU=0 Radius=16 StartAngle=5.60905 EndAngle=6.28319
    g7: LineSegment StartX=114 StartY=19 StartZ=0 EndX=114 EndY=35 EndZ=0
    g8: LineSegment StartX=110.5 StartY=9.01251 StartZ=0 EndX=114.163 EndY=9.01251 EndZ=0
    g9: LineSegment StartX=114 StartY=35 StartZ=0 EndX=19 EndY=35 EndZ=0
    g10: LineSegment StartX=0 StartY=3 StartZ=0 EndX=0 EndY=0 EndZ=0
    g11: LineSegment StartX=3 StartY=0 StartZ=0 EndX=0 EndY=0 EndZ=0
    g12: LineSegment StartX=3 StartY=19 StartZ=0 EndX=3 EndY=0 EndZ=0
  constraints (33):
    c: Vertical(g0)
    c: Distance(g0) = 19
    c: Block(g0)
    c: Coincident(g1,g0)
    c: Block(g1)
    c: Vertical(g2)
    c: Block(g2)
    c: Coincident(g3,g0)
    c: Horizontal(g3)
    c: Distance(g3) = 98
    c: Coincident(g4,g3)
    c: Coincident(g4,g2)
    c: Block(g4)
    c: Coincident(g5,g4)
    c: Coincident(g6,g1)
    c: Block(g6)
    c: Block(g5)
    c: Coincident(g7,g6)
    c: Vertical(g7)
    c: Coincident(g8,g6)
    c: Coincident(g8,g1)
    c: Coincident(g9,g7)
    c: Coincident(g9,g5)
    c: Horizontal(g9)
    c: Tangent(g9,g5)
    c: Coincident(g10,g2)
    c: Distance(g10) = 3
    c: Vertical(g10)
    c: Coincident(g11,g10)
    c: Horizontal(g11)
    c: Coincident(g12,g5)
    c: Coincident(g12,g11)
    c: Vertical(g12)
FEATURE [Part::Extrusion] Extrude011  label="top006"
  Base = -> Sketch013
  Dir = (0,0,1)
  DirMode = 2
  FaceMakerClass = Part::FaceMakerBullseye
  LengthFwd = 72
  LengthRev = 0
  Solid = true
  Symmetric = false
FEATURE [Sketcher::SketchObject] Sketch014
  FullyConstrained = true
  MapMode = 3
  Placement = pos=(0,0,0) rot=(1,0,0;1.5708rad)
  Support = -> [Extrude011]
  sketch-geometry (8):
    g0: Circle CenterX=80.351 CenterY=-67.6202 CenterZ=0 NormalX=0 NormalY=0 NormalZ=1 AngleXU=0 Radius=2
    g1: Circle CenterX=80.351 CenterY=-67.6202 CenterZ=0 NormalX=0 NormalY=0 NormalZ=1 AngleXU=0 Radius=3
    g2: Circle CenterX=80.351 CenterY=-4.92017 CenterZ=0 NormalX=0 NormalY=0 NormalZ=1 AngleXU=0 Radius=2
    g3: Circle CenterX=80.351 CenterY=-4.92017 CenterZ=0 NormalX=0 NormalY=0 NormalZ=1 AngleXU=0 Radius=3
    g4: Circle CenterX=23.851 CenterY=-4.92017 CenterZ=0 NormalX=0 NormalY=0 NormalZ=1 AngleXU=0 Radius=2
    g5: Circle CenterX=23.851 CenterY=-4.92017 CenterZ=0 NormalX=0 NormalY=0 NormalZ=1 AngleXU=0 Radius=3
    g6: Circle CenterX=23.851 CenterY=-67.6202 CenterZ=0 NormalX=0 NormalY=0 NormalZ=1 AngleXU=0 Radius=2
    g7: Circle CenterX=23.851 CenterY=-67.6202 CenterZ=0 NormalX=0 NormalY=0 NormalZ=1 AngleXU=0 Radius=3
  constraints (8):
    c: Block(g3)
    c: Block(g2)
    c: Block(g1)
    c: Block(g0)
    c: Block(g6)
    c: Block(g7)
    c: Block(g4)
    c: Block(g5)
FEATURE [Part::Feature] Face027
  shape: bbox 11 x 6 x 2e-07 mm, 1 faces, 0 solids (baked)
FEATURE [Part::Revolution] Revolve027
  Angle = 360
  Axis = (0,1,0)
  Base = (0,0,0)
  FaceMakerClass = Part::FaceMakerBullseye
  Placement = pos=(30.3,-1,51.7) rot=(0,0,1;0rad)
  Solid = false
  Source = -> Face027
  Symmetric = false
FEATURE [Part::Feature] Face028
  shape: bbox 11 x 6 x 2e-07 mm, 1 faces, 0 solids (baked)
FEATURE [Part::Revolution] Revolve028
  Angle = 360
  Axis = (0,1,0)
  Base = (0,0,0)
  FaceMakerClass = Part::FaceMakerBullseye
  Placement = pos=(62.3,-1,19.7) rot=(0,0,1;0rad)
  Solid = false
  Source = -> Face028
  Symmetric = false
FEATURE [Part::Feature] Face029
  shape: bbox 11 x 6 x 2e-07 mm, 1 faces, 0 solids (baked)
FEATURE [Part::Revolution] Revolve029
  Angle = 360
  Axis = (0,1,0)
  Base = (0,0,0)
  FaceMakerClass = Part::FaceMakerBullseye
  Placement = pos=(62.3,-1,51.7) rot=(0,0,1;0rad)
  Solid = false
  Source = -> Face029
  Symmetric = false
FEATURE [Part::Feature] Wire
  shape: bbox 11 x 5.2 x 2e-07 mm, 0 faces, 0 solids (baked)
FEATURE [Part::Revolution] Revolve030
  Angle = 360
  Axis = (0,1,0)
  Base = (0,0,0)
  FaceMakerClass = Part::FaceMakerBullseye
  Placement = pos=(30.3,38,19.7) rot=(0,0,1;0rad)
  Solid = true
  Source = -> Wire
  Symmetric = false
FEATURE [Part::Feature] Wire001
  shape: bbox 11 x 5.2 x 2e-07 mm, 0 faces, 0 solids (baked)
FEATURE [Part::Revolution] Revolve031
  Angle = 360
  Axis = (0,1,0)
  Base = (0,0,0)
  FaceMakerClass = Part::FaceMakerBullseye
  Placement = pos=(30.3,38,51.7) rot=(0,0,1;0rad)
  Solid = true
  Source = -> Wire001
  Symmetric = false
FEATURE [Part::Feature] Wire002
  shape: bbox 11 x 5.2 x 2e-07 mm, 0 faces, 0 solids (baked)
FEATURE [Part::Revolution] Revolve032
  Angle = 360
  Axis = (0,1,0)
  Base = (0,0,0)
  FaceMakerClass = Part::FaceMakerBullseye
  Placement = pos=(62.3,38,51.7) rot=(0,0,1;0rad)
  Solid = true
  Source = -> Wire002
  Symmetric = false
FEATURE [Part::Feature] Wire003
  shape: bbox 11 x 5.2 x 2e-07 mm, 0 faces, 0 solids (baked)
FEATURE [Part::Revolution] Revolve033
  Angle = 360
  Axis = (0,1,0)
  Base = (0,0,0)
  FaceMakerClass = Part::FaceMakerBullseye
  Placement = pos=(62.3,38,19.7) rot=(0,0,1;0rad)
  Solid = true
  Source = -> Wire003
  Symmetric = false
FEATURE [Part::MultiFuse] Fusion045  label="altRandScrewHousing"
  Shapes = -> [Revolve029,Revolve027,Revolve028,Revolve026]
FEATURE [Part::MultiFuse] Fusion046  label="fanScrewHousing"
  Shapes = -> [Revolve033,Revolve032,Revolve031,Revolve030]
FEATURE [Sketcher::SketchObject] Sketch015
  FullyConstrained = true
  sketch-geometry (17):
    g0: Circle CenterX=-3.5 CenterY=23.5 CenterZ=0 NormalX=0 NormalY=0 NormalZ=1 AngleXU=0 Radius=1
    g1: Circle CenterX=-1 CenterY=15.25 CenterZ=0 NormalX=0 NormalY=0 NormalZ=1 AngleXU=0 Radius=1
    g2: Circle CenterX=-3.5 CenterY=7 CenterZ=0 NormalX=0 NormalY=0 NormalZ=1 AngleXU=0 Radius=1
    g3: BSplineCurve PolesCount=3 KnotsCount=2 Degree=2 IsPeriodic=0
    g4: GeomPoint X=-3.5 Y=23.5 Z=0
    g5: GeomPoint X=-3.5 Y=7 Z=0
    g6: Circle CenterX=-4.8 CenterY=30.5 CenterZ=0 NormalX=0 NormalY=0 NormalZ=1 AngleXU=0 Radius=1
    g7: Circle CenterX=-3.5 CenterY=30.5 CenterZ=0 NormalX=0 NormalY=0 NormalZ=1 AngleXU=0 Radius=1
    g8: Circle CenterX=-3.5 CenterY=29.2 CenterZ=0 NormalX=0 NormalY=0 NormalZ=1 AngleXU=0 Radius=1
    g9: BSplineCurve PolesCount=3 KnotsCount=2 Degree=2 IsPeriodic=0
    g10: GeomPoint X=-4.8 Y=30.5 Z=0
    g11: GeomPoint X=-3.5 Y=29.2 Z=0
    g12: LineSegment StartX=-3.5 StartY=29.2 StartZ=0 EndX=-3.5 EndY=23.5 EndZ=0
    g13: LineSegment StartX=-4.8 StartY=30.5 StartZ=0 EndX=0 EndY=30.5 EndZ=0
    g14: LineSegment StartX=-3.5 StartY=0.3 StartZ=0 EndX=0 EndY=0.3 EndZ=0
    g15: LineSegment StartX=-3.5 StartY=0.3 StartZ=0 EndX=-3.5 EndY=7 EndZ=0
    g16: LineSegment StartX=0 StartY=0.3 StartZ=0 EndX=0 EndY=30.5 EndZ=0
  constraints (33):
    c: Weight(g0) = 1
    c: Equal(g0,g1)
    c: Equal(g0,g2)
    c: InternalAlignment(g0,g3)
    c: InternalAlignment(g1,g3)
    c: InternalAlignment(g2,g3)
    c: InternalAlignment(g4,g3)
    c: InternalAlignment(g5,g3)
    c: Block(g3)
    c: Weight(g6) = 1
    c: Equal(g6,g7)
    c: Equal(g6,g8)
    c: InternalAlignment(g6,g9)
    c: InternalAlignment(g7,g9)
    c: InternalAlignment(g8,g9)
    c: InternalAlignment(g10,g9)
    c: InternalAlignment(g11,g9)
    c: Block(g9)
    c: Coincident(g12,g9)
    c: Coincident(g12,g3)
    c: Vertical(g12)
    c: Coincident(g13,g9)
    c: Horizontal(g13)
    c: Distance(g13) = 4.8
    c: Horizontal(g14)
    c: Block(g14)
    c: Coincident(g15,g14)
    c: Coincident(g15,g3)
    c: Vertical(g15)
    c: Coincident(g16,g14)
    c: Coincident(g16,g13)
    c: Vertical(g16)
    c: Tangent(g16,g1)
FEATURE [Sketcher::SketchObject] Sketch016
  FullyConstrained = true
  sketch-geometry (16):
    g0: Circle CenterX=-3.5 CenterY=23.5 CenterZ=0 NormalX=0 NormalY=0 NormalZ=1 AngleXU=0 Radius=1
    g1: Circle CenterX=-1 CenterY=15.25 CenterZ=0 NormalX=0 NormalY=0 NormalZ=1 AngleXU=0 Radius=1
    g2: Circle CenterX=-3.5 CenterY=7 CenterZ=0 NormalX=0 NormalY=0 NormalZ=1 AngleXU=0 Radius=1
    g3: BSplineCurve PolesCount=3 KnotsCount=2 Degree=2 IsPeriodic=0
    g4: GeomPoint X=-3.5 Y=23.5 Z=0
    g5: GeomPoint X=-3.5 Y=7 Z=0
    g6: LineSegment StartX=-3.5 StartY=28.2 StartZ=0 EndX=-3.5 EndY=23.5 EndZ=0
    g7: LineSegment StartX=0 StartY=29.5 StartZ=0 EndX=0 EndY=30 EndZ=0
    g8: LineSegment StartX=-3.5 StartY=28.2 StartZ=0 EndX=-3.5 EndY=30 EndZ=0
    g9: LineSegment StartX=0 StartY=30 StartZ=0 EndX=0 EndY=30.5 EndZ=0
    g10: LineSegment StartX=0 StartY=30.5 StartZ=0 EndX=-3.5 EndY=30.5 EndZ=0
    g11: LineSegment StartX=-3.5 StartY=30.5 StartZ=0 EndX=-3.5 EndY=30 EndZ=0
    g12: LineSegment StartX=0 StartY=29.5 StartZ=0 EndX=0 EndY=5 EndZ=0
    g13: LineSegment StartX=-3.5 StartY=0.3 StartZ=0 EndX=-3.5 EndY=7 EndZ=0
    g14: LineSegment StartX=-3.5 StartY=0.3 StartZ=0 EndX=0 EndY=0.3 EndZ=0
    g15: LineSegment StartX=0 StartY=5 StartZ=0 EndX=0 EndY=0.3 EndZ=0
  constraints (39):
    c: Weight(g0) = 1
    c: Equal(g0,g1)
    c: Equal(g0,g2)
    c: InternalAlignment(g0,g3)
    c: InternalAlignment(g1,g3)
    c: InternalAlignment(g2,g3)
    c: InternalAlignment(g4,g3)
    c: InternalAlignment(g5,g3)
    c: Block(g3)
    c: Coincident(g6,g3)
    c: Vertical(g6)
    c: Vertical(g7)
    c: Distance(g7) = 0.5
    c: Coincident(g8,g6)
    c: Vertical(g8)
    c: Block(g6)
    c: Block(g7)
    c: Vertical(g9)
    c: Equal(g7,g9) = 0.5
    c: Block(g9)
    c: Coincident(g9,g7)
    c: Horizontal(g10)
    c: Coincident(g10,g9)
    c: Coincident(g11,g10)
    c: Coincident(g11,g8)
    c: Vertical(g11)
    c: Block(g11)
    c: Coincident(g12,g7)
    c: Vertical(g12)
    c: Coincident(g13,g3)
    c: Vertical(g13)
    c: Distance(g13) = 6.7
    c: Coincident(g14,g13)
    c: Horizontal(g14)
    c: Block(g14)
    c: Coincident(g15,g12)
    c: Coincident(g15,g14)
    c: Vertical(g15)
    c: Block(g15)
FEATURE [Sketcher::SketchObject] Sketch017
  FullyConstrained = true
  sketch-geometry (11):
    g0: LineSegment StartX=-3.5 StartY=1e-16 StartZ=0 EndX=-1.6 EndY=1e-16 EndZ=0
    g1: LineSegment StartX=-1.6 StartY=1e-16 StartZ=0 EndX=-1.6 EndY=1.5 EndZ=0
    g2: LineSegment StartX=-3.5 StartY=1.5 StartZ=0 EndX=-1.6 EndY=1.5 EndZ=0
    g3: LineSegment StartX=-3.5 StartY=1e-16 StartZ=0 EndX=-4.8 EndY=1e-16 EndZ=0
    g4: Circle CenterX=-3.5 CenterY=1.3 CenterZ=0 NormalX=0 NormalY=0 NormalZ=1 AngleXU=0 Radius=1
    g5: Circle CenterX=-3.5 CenterY=1e-16 CenterZ=0 NormalX=0 NormalY=0 NormalZ=1 AngleXU=0 Radius=1
    g6: Circle CenterX=-4.8 CenterY=1e-16 CenterZ=0 NormalX=0 NormalY=0 NormalZ=1 AngleXU=0 Radius=1
    g7: BSplineCurve PolesCount=3 KnotsCount=2 Degree=2 IsPeriodic=0
    g8: GeomPoint X=-3.5 Y=1.3 Z=0
    g9: GeomPoint X=-4.8 Y=1e-16 Z=0
    g10: LineSegment StartX=-3.5 StartY=1.3 StartZ=0 EndX=-3.5 EndY=1.5 EndZ=0
  constraints (24):
    c: Horizontal(g0)
    c: Distance(g0) = 1.9
    c: Block(g0)
    c: Coincident(g1,g0)
    c: Vertical(g1)
    c: Coincident(g2,g1)
    c: Horizontal(g2)
    c: Coincident(g3,g0)
    c: Horizontal(g3)
    c: Distance(g3) = 1.3
    c: Weight(g4) = 1
    c: Equal(g4,g5)
    c: Coincident(g5,g0)
    c: Equal(g4,g6)
    c: Coincident(g7,g3)
    c: InternalAlignment(g4,g7)
    c: InternalAlignment(g5,g7)
    c: InternalAlignment(g6,g7)
    c: InternalAlignment(g8,g7)
    c: InternalAlignment(g9,g7)
    c: Coincident(g10,g7)
    c: Coincident(g10,g2)
    c: Vertical(g10)
    c: Block(g10)
FEATURE [Part::Feature] Face035
  shape: bbox 3.2 x 1.5 x 2e-07 mm, 1 faces, 0 solids (baked)
FEATURE [Part::Revolution] Revolve039  label="backCaseScrewRetainer"
  Angle = 360
  Axis = (0,1,0)
  Base = (0,0,0)
  FaceMakerClass = Part::FaceMakerBullseye
  Placement = pos=(12.5,3,62) rot=(0,0,1;0rad)
  Solid = false
  Source = -> Face035
  Symmetric = false
FEATURE [Part::Feature] Face036
  shape: bbox 3.2 x 1.5 x 2e-07 mm, 1 faces, 0 solids (baked)
FEATURE [Part::Feature] Face039
  shape: bbox 4.8 x 30.2 x 2e-07 mm, 1 faces, 0 solids (baked)
FEATURE [Part::Revolution] Revolve043  label="frontCaseScrewPost002"
  Angle = 360
  Axis = (0,1,0)
  Base = (0,0,0)
  FaceMakerClass = Part::FaceMakerBullseye
  Placement = pos=(89.5,4.5,3.5) rot=(0,0,1;0rad)
  Solid = false
  Source = -> Face039
  Symmetric = false
FEATURE [Part::Feature] Face042
  shape: bbox 4.8 x 30.2 x 2e-07 mm, 1 faces, 0 solids (baked)
FEATURE [Part::Revolution] Revolve046  label="frontCaseScrewPost003"
  Angle = 360
  Axis = (0,1,0)
  Base = (0,0,0)
  FaceMakerClass = Part::FaceMakerBullseye
  Placement = pos=(89.5,4.5,68.5) rot=(0,0,1;0rad)
  Solid = false
  Source = -> Face042
  Symmetric = false
FEATURE [Part::Feature] Face043
  shape: bbox 3.2 x 1.5 x 2e-07 mm, 1 faces, 0 solids (baked)
FEATURE [Part::Revolution] Revolve047  label="frontCaseScrewRetainer002"
  Angle = 360
  Axis = (0,1,0)
  Base = (0,0,0)
  FaceMakerClass = Part::FaceMakerBullseye
  Placement = pos=(89.5,3,68.5) rot=(0,0,1;0rad)
  Solid = false
  Source = -> Face043
  Symmetric = false
FEATURE [Part::Feature] Face044
  shape: bbox 3.2 x 1.5 x 2e-07 mm, 1 faces, 0 solids (baked)
FEATURE [Part::Revolution] Revolve048  label="frontCaseScrewRetainer003"
  Angle = 360
  Axis = (0,1,0)
  Base = (0,0,0)
  FaceMakerClass = Part::FaceMakerBullseye
  Placement = pos=(89.5,3,3.5) rot=(0,0,1;0rad)
  Solid = false
  Source = -> Face044
  Symmetric = false
FEATURE [App::MeasureDistance] Distance002  label="Distance: 1.67 mm"
  Distance = 1.66921
  P1 = (99.2361,4.7524,71.7)
  P2 = (99.2347,6.42161,71.7)
FEATURE [Sketcher::SketchObject] Sketch018
  FullyConstrained = true
  sketch-geometry (7):
    g0: LineSegment StartX=0 StartY=0 StartZ=0 EndX=0 EndY=6 EndZ=0
    g1: Circle CenterX=0 CenterY=0 CenterZ=0 NormalX=0 NormalY=0 NormalZ=1 AngleXU=0 Radius=1
    g2: Circle CenterX=8 CenterY=6 CenterZ=0 NormalX=0 NormalY=0 NormalZ=1 AngleXU=0 Radius=1
    g3: BSplineCurve PolesCount=3 KnotsCount=2 Degree=2 IsPeriodic=0
    g4: GeomPoint X=0 Y=0 Z=0
    g5: GeomPoint X=8 Y=6 Z=0
    g6: LineSegment StartX=0 StartY=6 StartZ=0 EndX=8 EndY=6 EndZ=0
  constraints (14):
    c: Coincident(g0,g-1)
    c: Distance(g0) = 6
    c: Vertical(g0)
    c: Coincident(g3,g0)
    c: Weight(g1) = 1
    c: Equal(g1,g2)
    c: InternalAlignment(g1,g3)
    c: InternalAlignment(g2,g3)
    c: InternalAlignment(g4,g3)
    c: InternalAlignment(g5,g3)
    c: Block(g3)
    c: Coincident(g6,g0)
    c: Coincident(g6,g3)
    c: Horizontal(g6)
FEATURE [Part::Extrusion] Extrude012  label="caseScrewPillarBracket"
  Base = -> Sketch018
  Dir = (0,0,1)
  DirMode = 2
  FaceMakerClass = Part::FaceMakerBullseye
  LengthFwd = 2.4
  LengthRev = 0
  Placement = pos=(15.76,29,8.8) rot=(0,1,0;0rad)
  Solid = true
  Symmetric = false
FEATURE [Sketcher::SketchObject] Sketch019
  FullyConstrained = true
  sketch-geometry (7):
    g0: LineSegment StartX=0 StartY=0 StartZ=0 EndX=0 EndY=6 EndZ=0
    g1: Circle CenterX=0 CenterY=0 CenterZ=0 NormalX=0 NormalY=0 NormalZ=1 AngleXU=0 Radius=1
    g2: Circle CenterX=8 CenterY=6 CenterZ=0 NormalX=0 NormalY=0 NormalZ=1 AngleXU=0 Radius=1
    g3: BSplineCurve PolesCount=3 KnotsCount=2 Degree=2 IsPeriodic=0
    g4: GeomPoint X=0 Y=0 Z=0
    g5: GeomPoint X=8 Y=6 Z=0
    g6: LineSegment StartX=0 StartY=6 StartZ=0 EndX=8 EndY=6 EndZ=0
  constraints (14):
    c: Coincident(g0,g-1)
    c: Distance(g0) = 6
    c: Vertical(g0)
    c: Coincident(g3,g0)
    c: Weight(g1) = 1
    c: Equal(g1,g2)
    c: InternalAlignment(g1,g3)
    c: InternalAlignment(g2,g3)
    c: InternalAlignment(g4,g3)
    c: InternalAlignment(g5,g3)
    c: Block(g3)
    c: Coincident(g6,g0)
    c: Coincident(g6,g3)
    c: Horizontal(g6)
FEATURE [Part::Extrusion] Extrude013  label="caseScrewPillarBracket001"
  Base = -> Sketch019
  Dir = (0,0,1)
  DirMode = 2
  FaceMakerClass = Part::FaceMakerBullseye
  LengthFwd = 2.4
  LengthRev = 0
  Placement = pos=(15.76,29,60.8) rot=(0,0,1;0rad)
  Solid = true
  Symmetric = false
FEATURE [Sketcher::SketchObject] Sketch020
  FullyConstrained = true
  sketch-geometry (7):
    g0: LineSegment StartX=0 StartY=0 StartZ=0 EndX=0 EndY=6 EndZ=0
    g1: Circle CenterX=0 CenterY=0 CenterZ=0 NormalX=0 NormalY=0 NormalZ=1 AngleXU=0 Radius=1
    g2: Circle CenterX=8 CenterY=6 CenterZ=0 NormalX=0 NormalY=0 NormalZ=1 AngleXU=0 Radius=1
    g3: BSplineCurve PolesCount=3 KnotsCount=2 Degree=2 IsPeriodic=0
    g4: GeomPoint X=0 Y=0 Z=0
    g5: GeomPoint X=8 Y=6 Z=0
    g6: LineSegment StartX=0 StartY=6 StartZ=0 EndX=8 EndY=6 EndZ=0
  constraints (14):
    c: Coincident(g0,g-1)
    c: Distance(g0) = 6
    c: Vertical(g0)
    c: Coincident(g3,g0)
    c: Weight(g1) = 1
    c: Equal(g1,g2)
    c: InternalAlignment(g1,g3)
    c: InternalAlignment(g2,g3)
    c: InternalAlignment(g4,g3)
    c: InternalAlignment(g5,g3)
    c: Block(g3)
    c: Coincident(g6,g0)
    c: Coincident(g6,g3)
    c: Horizontal(g6)
FEATURE [Part::Extrusion] Extrude014  label="caseScrewPillarBracket002"
  Base = -> Sketch020
  Dir = (0,0,1)
  DirMode = 2
  FaceMakerClass = Part::FaceMakerBullseye
  LengthFwd = 2.4
  LengthRev = 0
  Placement = pos=(13.7,29,13.26) rot=(0,1,0;-1.5708rad)
  Solid = true
  Symmetric = false
FEATURE [Sketcher::SketchObject] Sketch021
  FullyConstrained = true
  sketch-geometry (7):
    g0: LineSegment StartX=0 StartY=0 StartZ=0 EndX=0 EndY=6 EndZ=0
    g1: Circle CenterX=0 CenterY=0 CenterZ=0 NormalX=0 NormalY=0 NormalZ=1 AngleXU=0 Radius=1
    g2: Circle CenterX=8 CenterY=6 CenterZ=0 NormalX=0 NormalY=0 NormalZ=1 AngleXU=0 Radius=1
    g3: BSplineCurve PolesCount=3 KnotsCount=2 Degree=2 IsPeriodic=0
    g4: GeomPoint X=0 Y=0 Z=0
    g5: GeomPoint X=8 Y=6 Z=0
    g6: LineSegment StartX=0 StartY=6 StartZ=0 EndX=8 EndY=6 EndZ=0
  constraints (14):
    c: Coincident(g0,g-1)
    c: Distance(g0) = 6
    c: Vertical(g0)
    c: Coincident(g3,g0)
    c: Weight(g1) = 1
    c: Equal(g1,g2)
    c: InternalAlignment(g1,g3)
    c: InternalAlignment(g2,g3)
    c: InternalAlignment(g4,g3)
    c: InternalAlignment(g5,g3)
    c: Block(g3)
    c: Coincident(g6,g0)
    c: Coincident(g6,g3)
    c: Horizontal(g6)
FEATURE [Part::Extrusion] Extrude015  label="caseScrewPillarBracket003"
  Base = -> Sketch021
  Dir = (0,0,1)
  DirMode = 2
  FaceMakerClass = Part::FaceMakerBullseye
  LengthFwd = 2.4
  LengthRev = 0
  Placement = pos=(11.3,29,58.74) rot=(0,1,0;1.5708rad)
  Solid = true
  Symmetric = false
FEATURE [Sketcher::SketchObject] Sketch022
  FullyConstrained = true
  sketch-geometry (7):
    g0: LineSegment StartX=0 StartY=0 StartZ=0 EndX=0 EndY=6 EndZ=0
    g1: Circle CenterX=0 CenterY=0 CenterZ=0 NormalX=0 NormalY=0 NormalZ=1 AngleXU=0 Radius=1
    g2: Circle CenterX=8 CenterY=6 CenterZ=0 NormalX=0 NormalY=0 NormalZ=1 AngleXU=0 Radius=1
    g3: BSplineCurve PolesCount=3 KnotsCount=2 Degree=2 IsPeriodic=0
    g4: GeomPoint X=0 Y=0 Z=0
    g5: GeomPoint X=8 Y=6 Z=0
    g6: LineSegment StartX=0 StartY=6 StartZ=0 EndX=8 EndY=6 EndZ=0
  constraints (14):
    c: Coincident(g0,g-1)
    c: Distance(g0) = 6
    c: Vertical(g0)
    c: Coincident(g3,g0)
    c: Weight(g1) = 1
    c: Equal(g1,g2)
    c: InternalAlignment(g1,g3)
    c: InternalAlignment(g2,g3)
    c: InternalAlignment(g4,g3)
    c: InternalAlignment(g5,g3)
    c: Block(g3)
    c: Coincident(g6,g0)
    c: Coincident(g6,g3)
    c: Horizontal(g6)
FEATURE [Part::Extrusion] Extrude016  label="caseScrewPillarBracket004"
  Base = -> Sketch022
  Dir = (0,0,1)
  DirMode = 2
  FaceMakerClass = Part::FaceMakerBullseye
  LengthFwd = 2.4
  LengthRev = 0
  Placement = pos=(88.3,29,65.23) rot=(0,1,0;1.5708rad)
  Solid = true
  Symmetric = false
FEATURE [Sketcher::SketchObject] Sketch023
  FullyConstrained = true
  sketch-geometry (7):
    g0: LineSegment StartX=0 StartY=0 StartZ=0 EndX=0 EndY=6 EndZ=0
    g1: Circle CenterX=0 CenterY=0 CenterZ=0 NormalX=0 NormalY=0 NormalZ=1 AngleXU=0 Radius=1
    g2: Circle CenterX=8 CenterY=6 CenterZ=0 NormalX=0 NormalY=0 NormalZ=1 AngleXU=0 Radius=1
    g3: BSplineCurve PolesCount=3 KnotsCount=2 Degree=2 IsPeriodic=0
    g4: GeomPoint X=0 Y=0 Z=0
    g5: GeomPoint X=8 Y=6 Z=0
    g6: LineSegment StartX=0 StartY=6 StartZ=0 EndX=8 EndY=6 EndZ=0
  constraints (14):
    c: Coincident(g0,g-1)
    c: Distance(g0) = 6
    c: Vertical(g0)
    c: Coincident(g3,g0)
    c: Weight(g1) = 1
    c: Equal(g1,g2)
    c: InternalAlignment(g1,g3)
    c: InternalAlignment(g2,g3)
    c: InternalAlignment(g4,g3)
    c: InternalAlignment(g5,g3)
    c: Block(g3)
    c: Coincident(g6,g0)
    c: Coincident(g6,g3)
    c: Horizontal(g6)
FEATURE [Part::Extrusion] Extrude017  label="caseScrewPillarBracket005"
  Base = -> Sketch023
  Dir = (0,0,1)
  DirMode = 2
  FaceMakerClass = Part::FaceMakerBullseye
  LengthFwd = 2.4
  LengthRev = 0
  Placement = pos=(90.7,29,6.77) rot=(0,-1,0;1.5708rad)
  Solid = true
  Symmetric = false
FEATURE [Sketcher::SketchObject] Sketch024
  FullyConstrained = true
  sketch-geometry (7):
    g0: LineSegment StartX=0 StartY=0 StartZ=0 EndX=0 EndY=6 EndZ=0
    g1: Circle CenterX=0 CenterY=0 CenterZ=0 NormalX=0 NormalY=0 NormalZ=1 AngleXU=0 Radius=1
    g2: Circle CenterX=8 CenterY=6 CenterZ=0 NormalX=0 NormalY=0 NormalZ=1 AngleXU=0 Radius=1
    g3: BSplineCurve PolesCount=3 KnotsCount=2 Degree=2 IsPeriodic=0
    g4: GeomPoint X=0 Y=0 Z=0
    g5: GeomPoint X=8 Y=6 Z=0
    g6: LineSegment StartX=0 StartY=6 StartZ=0 EndX=8 EndY=6 EndZ=0
  constraints (14):
    c: Coincident(g0,g-1)
    c: Distance(g0) = 6
    c: Vertical(g0)
    c: Coincident(g3,g0)
    c: Weight(g1) = 1
    c: Equal(g1,g2)
    c: InternalAlignment(g1,g3)
    c: InternalAlignment(g2,g3)
    c: InternalAlignment(g4,g3)
    c: InternalAlignment(g5,g3)
    c: Block(g3)
    c: Coincident(g6,g0)
    c: Coincident(g6,g3)
    c: Horizontal(g6)
FEATURE [Part::Extrusion] Extrude018  label="caseScrewPillarBracket006"
  Base = -> Sketch024
  Dir = (0,0,1)
  DirMode = 2
  FaceMakerClass = Part::FaceMakerBullseye
  LengthFwd = 2.4
  LengthRev = 0
  Placement = pos=(103.7,29,6.77) rot=(0,-1,0;1.5708rad)
  Solid = true
  Symmetric = false
FEATURE [Sketcher::SketchObject] Sketch025
  FullyConstrained = true
  sketch-geometry (7):
    g0: LineSegment StartX=0 StartY=0 StartZ=0 EndX=0 EndY=6 EndZ=0
    g1: Circle CenterX=0 CenterY=0 CenterZ=0 NormalX=0 NormalY=0 NormalZ=1 AngleXU=0 Radius=1
    g2: Circle CenterX=8 CenterY=6 CenterZ=0 NormalX=0 NormalY=0 NormalZ=1 AngleXU=0 Radius=1
    g3: BSplineCurve PolesCount=3 KnotsCount=2 Degree=2 IsPeriodic=0
    g4: GeomPoint X=0 Y=0 Z=0
    g5: GeomPoint X=8 Y=6 Z=0
    g6: LineSegment StartX=0 StartY=6 StartZ=0 EndX=8 EndY=6 EndZ=0
  constraints (14):
    c: Coincident(g0,g-1)
    c: Distance(g0) = 6
    c: Vertical(g0)
    c: Coincident(g3,g0)
    c: Weight(g1) = 1
    c: Equal(g1,g2)
    c: InternalAlignment(g1,g3)
    c: InternalAlignment(g2,g3)
    c: InternalAlignment(g4,g3)
    c: InternalAlignment(g5,g3)
    c: Block(g3)
    c: Coincident(g6,g0)
    c: Coincident(g6,g3)
    c: Horizontal(g6)
FEATURE [Part::Extrusion] Extrude019  label="caseScrewPillarBracket007"
  Base = -> Sketch025
  Dir = (0,0,1)
  DirMode = 2
  FaceMakerClass = Part::FaceMakerBullseye
  LengthFwd = 2.4
  LengthRev = 0
  Placement = pos=(101.3,29,65.23) rot=(0,1,0;1.5708rad)
  Solid = true
  Symmetric = false
FEATURE [Part::Box] Box011  label="frontCaseScrewPillarBracket"
  AttacherType = Attacher::AttachEngine3D
  Height = 2.4
  Length = 16
  Placement = pos=(87,28,2.3) rot=(0,0,1;0rad)
  Width = 7
FEATURE [Part::Box] Box012  label="frontCaseScrewPillarBracket001"
  AttacherType = Attacher::AttachEngine3D
  Height = 2.4
  Length = 16
  Placement = pos=(87,28,67.3) rot=(0,0,1;0rad)
  Width = 7
FEATURE [Sketcher::SketchObject] Sketch026
  FullyConstrained = true
  sketch-geometry (17):
    g0: Circle CenterX=-3.5 CenterY=23.5 CenterZ=0 NormalX=0 NormalY=0 NormalZ=1 AngleXU=0 Radius=1
    g1: Circle CenterX=-1 CenterY=15.25 CenterZ=0 NormalX=0 NormalY=0 NormalZ=1 AngleXU=0 Radius=1
    g2: Circle CenterX=-3.5 CenterY=7 CenterZ=0 NormalX=0 NormalY=0 NormalZ=1 AngleXU=0 Radius=1
    g3: BSplineCurve PolesCount=3 KnotsCount=2 Degree=2 IsPeriodic=0
    g4: GeomPoint X=-3.5 Y=23.5 Z=0
    g5: GeomPoint X=-3.5 Y=7 Z=0
    g6: Circle CenterX=-4.8 CenterY=30.5 CenterZ=0 NormalX=0 NormalY=0 NormalZ=1 AngleXU=0 Radius=1
    g7: Circle CenterX=-3.5 CenterY=30.5 CenterZ=0 NormalX=0 NormalY=0 NormalZ=1 AngleXU=0 Radius=1
    g8: Circle CenterX=-3.5 CenterY=29.2 CenterZ=0 NormalX=0 NormalY=0 NormalZ=1 AngleXU=0 Radius=1
    g9: BSplineCurve PolesCount=3 KnotsCount=2 Degree=2 IsPeriodic=0
    g10: GeomPoint X=-4.8 Y=30.5 Z=0
    g11: GeomPoint X=-3.5 Y=29.2 Z=0
    g12: LineSegment StartX=-3.5 StartY=29.2 StartZ=0 EndX=-3.5 EndY=23.5 EndZ=0
    g13: LineSegment StartX=-4.8 StartY=30.5 StartZ=0 EndX=0 EndY=30.5 EndZ=0
    g14: LineSegment StartX=-3.5 StartY=5 StartZ=0 EndX=-3.5 EndY=7 EndZ=0
    g15: LineSegment StartX=0 StartY=5 StartZ=0 EndX=0 EndY=30.5 EndZ=0
    g16: LineSegment StartX=-3.5 StartY=5 StartZ=0 EndX=0 EndY=5 EndZ=0
  constraints (33):
    c: Weight(g0) = 1
    c: Equal(g0,g1)
    c: Equal(g0,g2)
    c: InternalAlignment(g0,g3)
    c: InternalAlignment(g1,g3)
    c: InternalAlignment(g2,g3)
    c: InternalAlignment(g4,g3)
    c: InternalAlignment(g5,g3)
    c: Block(g3)
    c: Weight(g6) = 1
    c: Equal(g6,g7)
    c: Equal(g6,g8)
    c: InternalAlignment(g6,g9)
    c: InternalAlignment(g7,g9)
    c: InternalAlignment(g8,g9)
    c: InternalAlignment(g10,g9)
    c: InternalAlignment(g11,g9)
    c: Block(g9)
    c: Coincident(g12,g9)
    c: Coincident(g12,g3)
    c: Vertical(g12)
    c: Coincident(g13,g9)
    c: Horizontal(g13)
    c: Distance(g13) = 4.8
    c: Coincident(g14,g3)
    c: Vertical(g14)
    c: Coincident(g15,g13)
    c: Vertical(g15)
    c: Tangent(g15,g1)
    c: Distance(g14) = 2
    c: Coincident(g16,g14)
    c: Horizontal(g16)
    c: Coincident(g15,g16)
FEATURE [Part::Feature] Face050
  shape: bbox 4.8 x 25.5 x 2e-07 mm, 1 faces, 0 solids (baked)
FEATURE [Part::Revolution] Revolve054  label="moreFrontCaseScrewPost001"
  Angle = 360
  Axis = (0,1,0)
  Base = (0,0,0)
  FaceMakerClass = Part::FaceMakerBullseye
  Placement = pos=(102.5,4.5,3.5) rot=(0,0,1;0rad)
  Solid = false
  Source = -> Face050
  Symmetric = false
FEATURE [Part::Feature] Face051
  shape: bbox 4.8 x 25.5 x 2e-07 mm, 1 faces, 0 solids (baked)
FEATURE [Part::Revolution] Revolve055  label="moreFrontCaseScrewPost002"
  Angle = 360
  Axis = (0,1,0)
  Base = (0,0,0)
  FaceMakerClass = Part::FaceMakerBullseye
  Placement = pos=(102.5,4.5,68.5) rot=(0,0,1;0rad)
  Solid = false
  Source = -> Face051
  Symmetric = false
FEATURE [Sketcher::SketchObject] Sketch027
  FullyConstrained = true
  sketch-geometry (10):
    g0: LineSegment StartX=-1.6 StartY=4.7 StartZ=0 EndX=-1.6 EndY=1.7 EndZ=0
    g1: LineSegment StartX=-3.5 StartY=4.7 StartZ=0 EndX=-1.6 EndY=4.7 EndZ=0
    g2: LineSegment StartX=-1.6 StartY=1.7 StartZ=0 EndX=-1.6 EndY=1.5 EndZ=0
    g3: LineSegment StartX=-1.6 StartY=1.5 StartZ=0 EndX=-5.2 EndY=1.5 EndZ=0
    g4: Circle CenterX=-3.5 CenterY=4.7 CenterZ=0 NormalX=0 NormalY=0 NormalZ=1 AngleXU=0 Radius=1
    g5: Circle CenterX=-3.59627 CenterY=2.99743 CenterZ=0 NormalX=0 NormalY=0 NormalZ=1 AngleXU=0 Radius=1
    g6: Circle CenterX=-5.2 CenterY=1.5 CenterZ=0 NormalX=0 NormalY=0 NormalZ=1 AngleXU=0 Radius=1
    g7: BSplineCurve PolesCount=3 KnotsCount=2 Degree=2 IsPeriodic=0
    g8: GeomPoint X=-3.5 Y=4.7 Z=0
    g9: GeomPoint X=-5.2 Y=1.5 Z=0
  constraints (23):
    c: Vertical(g0)
    c: Distance(g0) = 3
    c: Coincident(g1,g0)
    c: Horizontal(g1)
    c: Block(g0)
    c: Block(g1)
    c: Coincident(g2,g0)
    c: Vertical(g2)
    c: Distance(g2) = 0.2
    c: Coincident(g3,g2)
    c: Horizontal(g3)
    c: Block(g3)
    c: Coincident(g7,g1)
    c: Weight(g4) = 1
    c: Equal(g4,g5)
    c: Equal(g4,g6)
    c: Coincident(g7,g3)
    c: InternalAlignment(g4,g7)
    c: InternalAlignment(g5,g7)
    c: InternalAlignment(g6,g7)
    c: InternalAlignment(g8,g7)
    c: InternalAlignment(g9,g7)
    c: Block(g7)
FEATURE [Sketcher::SketchObject] Sketch028
  FullyConstrained = true
  sketch-geometry (18):
    g0: LineSegment StartX=0 StartY=3e-16 StartZ=0 EndX=0 EndY=1.7 EndZ=0
    g1: LineSegment StartX=-3.5 StartY=0 StartZ=0 EndX=-3.5 EndY=0.9 EndZ=0
    g2: Circle CenterX=-2.7 CenterY=1.7 CenterZ=0 NormalX=0 NormalY=0 NormalZ=1 AngleXU=0 Radius=1
    g3: Circle CenterX=-3.5 CenterY=1.7 CenterZ=0 NormalX=0 NormalY=0 NormalZ=1 AngleXU=0 Radius=1
    g4: Circle CenterX=-3.5 CenterY=0.9 CenterZ=0 NormalX=0 NormalY=0 NormalZ=1 AngleXU=0 Radius=1
    g5: BSplineCurve PolesCount=3 KnotsCount=2 Degree=2 IsPeriodic=0
    g6: GeomPoint X=-2.7 Y=1.7 Z=0
    g7: GeomPoint X=-3.5 Y=0.9 Z=0
    g8: LineSegment StartX=-3.5 StartY=0 StartZ=0 EndX=-3.5 EndY=-7 EndZ=0
    g9: LineSegment StartX=0 StartY=3e-16 StartZ=0 EndX=0 EndY=-7 EndZ=0
    g10: LineSegment StartX=-3.5 StartY=-7 StartZ=0 EndX=0 EndY=-7 EndZ=0
    g11: LineSegment StartX=-2.7 StartY=1.7 StartZ=0 EndX=-1.6 EndY=1.7 EndZ=0
    g12: LineSegment StartX=0 StartY=1.7 StartZ=0 EndX=0 EndY=4.5 EndZ=0
    g13: LineSegment StartX=0 StartY=4.5 StartZ=0 EndX=0 EndY=10.8 EndZ=0
    g14: LineSegment StartX=0 StartY=10.8 StartZ=0 EndX=-2 EndY=10.8 EndZ=0
    g15: LineSegment StartX=-1.6 StartY=4.7 StartZ=0 EndX=-1.6 EndY=1.7 EndZ=0
    g16: LineSegment StartX=-1.6 StartY=4.7 StartZ=0 EndX=-2 EndY=4.7 EndZ=0
    g17: LineSegment StartX=-2 StartY=4.7 StartZ=0 EndX=-2 EndY=10.8 EndZ=0
  constraints (44):
    c: Vertical(g0)
    c: Vertical(g1)
    c: Distance(g1) = 0.9
    c: Block(g0)
    c: Distance(g0) = 1.7
    c: Weight(g2) = 1
    c: Equal(g2,g3)
    c: Equal(g2,g4)
    c: Coincident(g5,g1)
    c: InternalAlignment(g2,g5)
    c: InternalAlignment(g3,g5)
    c: InternalAlignment(g4,g5)
    c: InternalAlignment(g6,g5)
    c: InternalAlignment(g7,g5)
    c: Block(g5)
    c: Coincident(g8,g1)
    c: Vertical(g8)
    c: Distance(g8) = 7
    c: Vertical(g9)
    c: Equal(g8,g9) = 7
    c: Coincident(g9,g0)
    c: Coincident(g10,g8)
    c: Coincident(g10,g9)
    c: Horizontal(g10)
    c: Coincident(g11,g5)
    c: Horizontal(g11)
    c: Coincident(g12,g0)
    c: Vertical(g12)
    c: Distance(g12) = 2.8
    c: Coincident(g13,g12)
    c: Vertical(g13)
    c: Distance(g13) = 6.3
    c: Coincident(g14,g13)
    c: Horizontal(g14)
    c: Distance(g14) = 2
    c: Vertical(g15)
    c: Distance(g15) = 3
    c: Block(g11)
    c: Coincident(g15,g11)
    c: Coincident(g16,g15)
    c: Horizontal(g16)
    c: Coincident(g17,g16)
    c: Coincident(g17,g14)
    c: Vertical(g17)
FEATURE [Part::Revolution] Revolve040  label="backCaseScrewRetainer001"
  Angle = 360
  Axis = (0,1,0)
  Base = (0,0,0)
  FaceMakerClass = Part::FaceMakerBullseye
  Placement = pos=(12.5,3,10) rot=(0,0,1;0rad)
  Solid = false
  Source = -> Face036
  Symmetric = false
FEATURE [Part::Feature] Face055
  shape: bbox 3.5 x 30.2 x 2e-07 mm, 1 faces, 0 solids (baked)
FEATURE [Part::Revolution] Revolve059  label="backCaseScrewPost"
  Angle = 360
  Axis = (0,1,0)
  Base = (0,0,0)
  FaceMakerClass = Part::FaceMakerBullseye
  Placement = pos=(12.5,4.5,10) rot=(0,0,1;0rad)
  Solid = false
  Source = -> Face055
  Symmetric = false
FEATURE [Part::Feature] Face056
  shape: bbox 3.5 x 30.2 x 2e-07 mm, 1 faces, 0 solids (baked)
FEATURE [Part::Revolution] Revolve060  label="backCaseScrewPost001"
  Angle = 360
  Axis = (0,1,0)
  Base = (0,0,0)
  FaceMakerClass = Part::FaceMakerBullseye
  Placement = pos=(12.5,4.5,62) rot=(0,0,1;0rad)
  Solid = false
  Source = -> Face056
  Symmetric = false
FEATURE [Part::Feature] Face057
  shape: bbox 3.5 x 17.8 x 2e-07 mm, 1 faces, 0 solids (baked)
FEATURE [Part::Revolution] Revolve061  label="removeToCreateScrewAndThreadedInsertHole"
  Angle = 360
  Axis = (0,1,0)
  Base = (0,0,0)
  FaceMakerClass = Part::FaceMakerBullseye
  Placement = pos=(12.5,0,10) rot=(0,0,1;0rad)
  Solid = false
  Source = -> Face057
  Symmetric = false
FEATURE [Part::Feature] Face058
  shape: bbox 3.5 x 17.8 x 2e-07 mm, 1 faces, 0 solids (baked)
FEATURE [Part::Revolution] Revolve062  label="removeToCreateScrewAndThreadedInsertHole001"
  Angle = 360
  Axis = (0,1,0)
  Base = (0,0,0)
  FaceMakerClass = Part::FaceMakerBullseye
  Placement = pos=(12.5,0,62) rot=(0,0,1;0rad)
  Solid = false
  Source = -> Face058
  Symmetric = false
FEATURE [Part::Feature] Face059
  shape: bbox 3.5 x 17.8 x 2e-07 mm, 1 faces, 0 solids (baked)
FEATURE [Part::Revolution] Revolve063  label="removeToCreateScrewAndThreadedInsertHole002"
  Angle = 360
  Axis = (0,1,0)
  Base = (0,0,0)
  FaceMakerClass = Part::FaceMakerBullseye
  Placement = pos=(89.5,0,68.5) rot=(0,0,1;0rad)
  Solid = false
  Source = -> Face059
  Symmetric = false
FEATURE [Part::Feature] Face060
  shape: bbox 3.5 x 17.8 x 2e-07 mm, 1 faces, 0 solids (baked)
FEATURE [Part::Revolution] Revolve064  label="removeToCreateScrewAndThreadedInsertHole003"
  Angle = 360
  Axis = (0,1,0)
  Base = (0,0,0)
  FaceMakerClass = Part::FaceMakerBullseye
  Placement = pos=(89.5,0,3.5) rot=(0,0,1;0rad)
  Solid = false
  Source = -> Face060
  Symmetric = false
FEATURE [Part::Feature] Face061
  shape: bbox 3.5 x 17.8 x 2e-07 mm, 1 faces, 0 solids (baked)
FEATURE [Part::Revolution] Revolve065  label="removeToCreateScrewAndThreadedInsertHole004"
  Angle = 360
  Axis = (0,1,0)
  Base = (0,0,0)
  FaceMakerClass = Part::FaceMakerBullseye
  Placement = pos=(102.5,4.7,3.5) rot=(0,0,1;0rad)
  Solid = false
  Source = -> Face061
  Symmetric = false
FEATURE [Part::Feature] Face062
  shape: bbox 3.5 x 17.8 x 2e-07 mm, 1 faces, 0 solids (baked)
FEATURE [Part::Revolution] Revolve066  label="removeToCreateScrewAndThreadedInsertHole005"
  Angle = 360
  Axis = (0,1,0)
  Base = (0,0,0)
  FaceMakerClass = Part::FaceMakerBullseye
  Placement = pos=(102.5,4.7,68.5) rot=(0,0,1;0rad)
  Solid = false
  Source = -> Face062
  Symmetric = false
FEATURE [Part::MultiFuse] Fusion047  label="makeHoles"
  Shapes = -> [Revolve066,Revolve065,Revolve064,Revolve063,Revolve062,Revolve061]
FEATURE [Part::Feature] Face063
  shape: bbox 3.6 x 3.2 x 2e-07 mm, 1 faces, 0 solids (baked)
FEATURE [Part::Revolution] Revolve067  label="moreFrontCaseScrewRetainer002"
  Angle = 360
  Axis = (0,1,0)
  Base = (0,0,0)
  FaceMakerClass = Part::FaceMakerBullseye
  Placement = pos=(102.5,4.5,68.5) rot=(0,0,1;0rad)
  Solid = false
  Source = -> Face063
  Symmetric = false
FEATURE [Part::Feature] Face064
  shape: bbox 3.6 x 3.2 x 2e-07 mm, 1 faces, 0 solids (baked)
FEATURE [Part::Revolution] Revolve068  label="moreFrontCaseScrewRetainer003"
  Angle = 360
  Axis = (0,1,0)
  Base = (0,0,0)
  FaceMakerClass = Part::FaceMakerBullseye
  Placement = pos=(102.5,4.5,3.5) rot=(0,0,1;0rad)
  Solid = false
  Source = -> Face064
  Symmetric = false
FEATURE [Part::Cut] Cut014  label="bottom003"
  Base = -> Cut007
  Tool = -> Fusion047
FEATURE [Part::Feature] Face065
  shape: bbox 3.5 x 17.8 x 2e-07 mm, 1 faces, 0 solids (baked)
FEATURE [Part::Revolution] Revolve069  label="removeToCreateScrewAndThreadedInsertHole006"
  Angle = 360
  Axis = (0,1,0)
  Base = (0,0,0)
  FaceMakerClass = Part::FaceMakerBullseye
  Placement = pos=(12.5,0,10) rot=(0,0,1;0rad)
  Solid = false
  Source = -> Face065
  Symmetric = false
FEATURE [Part::Feature] Face066
  shape: bbox 3.5 x 17.8 x 2e-07 mm, 1 faces, 0 solids (baked)
FEATURE [Part::Revolution] Revolve070  label="removeToCreateScrewAndThreadedInsertHole007"
  Angle = 360
  Axis = (0,1,0)
  Base = (0,0,0)
  FaceMakerClass = Part::FaceMakerBullseye
  Placement = pos=(12.5,0,62) rot=(0,0,1;0rad)
  Solid = false
  Source = -> Face066
  Symmetric = false
FEATURE [Part::Feature] Face067
  shape: bbox 3.5 x 17.8 x 2e-07 mm, 1 faces, 0 solids (baked)
FEATURE [Part::Revolution] Revolve071  label="removeToCreateScrewAndThreadedInsertHole008"
  Angle = 360
  Axis = (0,1,0)
  Base = (0,0,0)
  FaceMakerClass = Part::FaceMakerBullseye
  Placement = pos=(89.5,0,68.5) rot=(0,0,1;0rad)
  Solid = false
  Source = -> Face067
  Symmetric = false
FEATURE [Part::Feature] Face068
  shape: bbox 3.5 x 17.8 x 2e-07 mm, 1 faces, 0 solids (baked)
FEATURE [Part::Revolution] Revolve072  label="removeToCreateScrewAndThreadedInsertHole009"
  Angle = 360
  Axis = (0,1,0)
  Base = (0,0,0)
  FaceMakerClass = Part::FaceMakerBullseye
  Placement = pos=(89.5,0,3.5) rot=(0,0,1;0rad)
  Solid = false
  Source = -> Face068
  Symmetric = false
FEATURE [Part::Feature] Face069
  shape: bbox 3.5 x 17.8 x 2e-07 mm, 1 faces, 0 solids (baked)
FEATURE [Part::Feature] Face070
  shape: bbox 3.5 x 17.8 x 2e-07 mm, 1 faces, 0 solids (baked)
FEATURE [Part::Revolution] Revolve073  label="removeToCreateScrewAndThreadedInsertHole010"
  Angle = 360
  Axis = (0,1,0)
  Base = (0,0,0)
  FaceMakerClass = Part::FaceMakerBullseye
  Placement = pos=(102.5,4.7,3.5) rot=(0,0,1;0rad)
  Solid = false
  Source = -> Face069
  Symmetric = false
FEATURE [Part::Revolution] Revolve074  label="removeToCreateScrewAndThreadedInsertHole011"
  Angle = 360
  Axis = (0,1,0)
  Base = (0,0,0)
  FaceMakerClass = Part::FaceMakerBullseye
  Placement = pos=(102.5,4.7,68.5) rot=(0,0,1;0rad)
  Solid = false
  Source = -> Face070
  Symmetric = false
FEATURE [Part::MultiFuse] Fusion048  label="makeHoles001"
  Shapes = -> [Revolve074,Revolve073,Revolve072,Revolve071,Revolve070,Revolve069]
FEATURE [Part::MultiFuse] Fusion049  label="caseScrewRetainers"
  Shapes = -> [Revolve067,Revolve068,Revolve048,Revolve047,Revolve039,Revolve040]
FEATURE [Part::Cut] Cut015  label="caseScrewRetainers001"
  Base = -> Fusion049
  Tool = -> Fusion048
FEATURE [Part::MultiFuse] Fusion050  label="casePillars"
  Shapes = -> [Revolve055,Revolve054,Revolve043,Revolve046,Revolve059,Revolve060]
FEATURE [Part::Feature] Face071 .. Face076  x6 (patterned run collapsed; names and placements below)
  shape: bbox 3.5 x 17.8 x 2e-07 mm, 1 faces, 0 solids (baked)
FEATURE [Part::Revolution] Revolve075  label="removeToCreateScrewAndThreadedInsertHole012"
  Angle = 360
  Axis = (0,1,0)
  Base = (0,0,0)
  FaceMakerClass = Part::FaceMakerBullseye
  Placement = pos=(12.5,0,10) rot=(0,0,1;0rad)
  Solid = false
  Source = -> Face071
  Symmetric = false
FEATURE [Part::Revolution] Revolve076  label="removeToCreateScrewAndThreadedInsertHole013"
  Angle = 360
  Axis = (0,1,0)
  Base = (0,0,0)
  FaceMakerClass = Part::FaceMakerBullseye
  Placement = pos=(12.5,0,62) rot=(0,0,1;0rad)
  Solid = false
  Source = -> Face072
  Symmetric = false
FEATURE [Part::Revolution] Revolve077  label="removeToCreateScrewAndThreadedInsertHole014"
  Angle = 360
  Axis = (0,1,0)
  Base = (0,0,0)
  FaceMakerClass = Part::FaceMakerBullseye
  Placement = pos=(89.5,0,68.5) rot=(0,0,1;0rad)
  Solid = false
  Source = -> Face073
  Symmetric = false
FEATURE [Part::Revolution] Revolve078  label="removeToCreateScrewAndThreadedInsertHole015"
  Angle = 360
  Axis = (0,1,0)
  Base = (0,0,0)
  FaceMakerClass = Part::FaceMakerBullseye
  Placement = pos=(89.5,0,3.5) rot=(0,0,1;0rad)
  Solid = false
  Source = -> Face074
  Symmetric = false
FEATURE [Part::Revolution] Revolve079  label="removeToCreateScrewAndThreadedInsertHole016"
  Angle = 360
  Axis = (0,1,0)
  Base = (0,0,0)
  FaceMakerClass = Part::FaceMakerBullseye
  Placement = pos=(102.5,4.7,3.5) rot=(0,0,1;0rad)
  Solid = false
  Source = -> Face075
  Symmetric = false
FEATURE [Part::Revolution] Revolve080  label="removeToCreateScrewAndThreadedInsertHole017"
  Angle = 360
  Axis = (0,1,0)
  Base = (0,0,0)
  FaceMakerClass = Part::FaceMakerBullseye
  Placement = pos=(102.5,4.7,68.5) rot=(0,0,1;0rad)
  Solid = false
  Source = -> Face076
  Symmetric = false
FEATURE [Part::MultiFuse] Fusion051  label="makeHoles002"
  Shapes = -> [Revolve080,Revolve079,Revolve078,Revolve077,Revolve076,Revolve075]
FEATURE [Part::Cut] Cut016  label="caesPillars"
  Base = -> Fusion050
  Tool = -> Fusion051
FEATURE [Part::Revolution] Revolve009  label="plugHousing016"
  Angle = 360
  Axis = (0,1,0)
  Base = (0,0,0)
  FaceMakerClass = Part::FaceMakerBullseye
  Placement = pos=(0,0,36.15) rot=(0,0,1;0rad)
  Solid = false
  Source = -> Face012
  Symmetric = false
FEATURE [Part::MultiFuse] Fusion014  label="plugHousing023"
  Placement = pos=(0,0,0) rot=(0,0,1;1.5708rad)
  Shapes = -> [Revolve011,Revolve009]
FEATURE [Part::Revolution] Revolve010  label="plugHousing017"
  Angle = 360
  Axis = (0,1,0)
  Base = (0,0,0)
  FaceMakerClass = Part::FaceMakerBullseye
  Placement = pos=(0,0,36.15) rot=(0,0,1;0rad)
  Solid = false
  Source = -> Face014
  Symmetric = false
FEATURE [Part::MultiFuse] Fusion015  label="plugHousing024"
  Placement = pos=(0,0,0) rot=(0,0,1;1.5708rad)
  Shapes = -> [Revolve010,Revolve015]
FEATURE [Part::Revolution] Revolve014  label="plugHousing026"
  Angle = 360
  Axis = (0,1,0)
  Base = (0,0,0)
  FaceMakerClass = Part::FaceMakerBullseye
  Placement = pos=(0,0,36.15) rot=(0,0,1;0rad)
  Solid = false
  Source = -> Face011
  Symmetric = false
FEATURE [Part::Revolution] Revolve013  label="plugHousing025"
  Angle = 360
  Axis = (0,1,0)
  Base = (0,0,0)
  FaceMakerClass = Part::FaceMakerBullseye
  Placement = pos=(0,0,36.15) rot=(0,0,1;0rad)
  Solid = false
  Source = -> Face015
  Symmetric = false
FEATURE [Part::MultiFuse] Fusion016  label="plugHousing028"
  Placement = pos=(0,19,0) rot=(0,0,1;3.14159rad)
  Shapes = -> [Fusion014,Fusion013]
FEATURE [Part::MultiFuse] Fusion011  label="plugHousing018"
  Placement = pos=(0,0,0) rot=(0,0,1;1.5708rad)
  Shapes = -> [Revolve014,Revolve013]
FEATURE [Part::MultiFuse] Fusion012  label="plugHousing019"
  Placement = pos=(0,19,0) rot=(0,0,1;3.14159rad)
  Shapes = -> [Fusion011,Fusion015]
FEATURE [Part::MultiFuse] Fusion017  label="plugHousing029"
  Placement = pos=(122.621,0,-0.15) rot=(0,0,1;0rad)
  Shapes = -> [Fusion016,Fusion012]
FEATURE [Part::MultiFuse] Fusion052  label="casePillarRetainers"
  Shapes = -> [Extrude012,Extrude013,Extrude014,Extrude015,Extrude016,Extrude017,Extrude018,Extrude019,Box011,Box012]
FEATURE [Part::Feature] Face077
  shape: bbox 3.5 x 17.8 x 2e-07 mm, 1 faces, 0 solids (baked)
FEATURE [Part::Revolution] Revolve081  label="removeToCreateScrewAndThreadedInsertHole018"
  Angle = 360
  Axis = (0,1,0)
  Base = (0,0,0)
  FaceMakerClass = Part::FaceMakerBullseye
  Placement = pos=(62.3,30.3,19.7) rot=(0,0,1;0rad)
  Solid = false
  Source = -> Face077
  Symmetric = false
FEATURE [Part::Feature] Face078
  shape: bbox 3.5 x 17.8 x 2e-07 mm, 1 faces, 0 solids (baked)
FEATURE [Part::Revolution] Revolve082  label="removeToCreateScrewAndThreadedInsertHole019"
  Angle = 360
  Axis = (0,1,0)
  Base = (0,0,0)
  FaceMakerClass = Part::FaceMakerBullseye
  Placement = pos=(62.3,30.3,51.7) rot=(0,0,1;0rad)
  Solid = false
  Source = -> Face078
  Symmetric = false
FEATURE [Part::Feature] Face079
  shape: bbox 3.5 x 17.8 x 2e-07 mm, 1 faces, 0 solids (baked)
FEATURE [Part::Revolution] Revolve083  label="removeToCreateScrewAndThreadedInsertHole020"
  Angle = 360
  Axis = (0,1,0)
  Base = (0,0,0)
  FaceMakerClass = Part::FaceMakerBullseye
  Placement = pos=(30.3,30.3,19.7) rot=(0,0,1;0rad)
  Solid = false
  Source = -> Face079
  Symmetric = false
FEATURE [Part::Feature] Face080
  shape: bbox 3.5 x 17.8 x 2e-07 mm, 1 faces, 0 solids (baked)
FEATURE [Part::Revolution] Revolve084  label="removeToCreateScrewAndThreadedInsertHole021"
  Angle = 360
  Axis = (0,1,0)
  Base = (0,0,0)
  FaceMakerClass = Part::FaceMakerBullseye
  Placement = pos=(30.3,30.3,51.7) rot=(0,0,1;0rad)
  Solid = false
  Source = -> Face080
  Symmetric = false
FEATURE [Part::MultiFuse] Fusion053  label="createThreadedInsertHolesForFan"
  Shapes = -> [Revolve081,Revolve082,Revolve083,Revolve084]
FEATURE [Part::Cut] Cut017  label="fanScrewHousing001"
  Base = -> Fusion046
  Tool = -> Fusion053
FEATURE [Part::Feature] Face081
  shape: bbox 3.5 x 17.8 x 2e-07 mm, 1 faces, 0 solids (baked)
FEATURE [Part::Revolution] Revolve085  label="removeToCreateScrewAndThreadedInsertHole022"
  Angle = 360
  Axis = (0,1,0)
  Base = (0,0,0)
  FaceMakerClass = Part::FaceMakerBullseye
  Placement = pos=(62.3,30.3,19.7) rot=(0,0,1;0rad)
  Solid = false
  Source = -> Face081
  Symmetric = false
FEATURE [Part::Feature] Face082
  shape: bbox 3.5 x 17.8 x 2e-07 mm, 1 faces, 0 solids (baked)
FEATURE [Part::Revolution] Revolve086  label="removeToCreateScrewAndThreadedInsertHole023"
  Angle = 360
  Axis = (0,1,0)
  Base = (0,0,0)
  FaceMakerClass = Part::FaceMakerBullseye
  Placement = pos=(62.3,30.3,51.7) rot=(0,0,1;0rad)
  Solid = false
  Source = -> Face082
  Symmetric = false
FEATURE [Part::Feature] Face083
  shape: bbox 3.5 x 17.8 x 2e-07 mm, 1 faces, 0 solids (baked)
FEATURE [Part::Revolution] Revolve087  label="removeToCreateScrewAndThreadedInsertHole024"
  Angle = 360
  Axis = (0,1,0)
  Base = (0,0,0)
  FaceMakerClass = Part::FaceMakerBullseye
  Placement = pos=(30.3,30.3,19.7) rot=(0,0,1;0rad)
  Solid = false
  Source = -> Face083
  Symmetric = false
FEATURE [Part::Feature] Face084
  shape: bbox 3.5 x 17.8 x 2e-07 mm, 1 faces, 0 solids (baked)
FEATURE [Part::Revolution] Revolve088  label="removeToCreateScrewAndThreadedInsertHole025"
  Angle = 360
  Axis = (0,1,0)
  Base = (0,0,0)
  FaceMakerClass = Part::FaceMakerBullseye
  Placement = pos=(30.3,30.3,51.7) rot=(0,0,1;0rad)
  Solid = false
  Source = -> Face084
  Symmetric = false
FEATURE [Part::MultiFuse] Fusion054  label="createThreadedInsertHolesForFan001"
  Shapes = -> [Revolve085,Revolve086,Revolve087,Revolve088]
FEATURE [Part::Cut] Cut018  label="top007"
  Base = -> Fusion040
  Tool = -> Fusion054
FEATURE [Sketcher::SketchObject] Sketch029
  FullyConstrained = false
  Placement = pos=(0,0,0) rot=(1,0,0;1.5708rad)
  sketch-geometry (24):
    g0: ArcOfCircle CenterX=-4 CenterY=-10.5 CenterZ=0 NormalX=0 NormalY=0 NormalZ=1 AngleXU=0 Radius=1.5 StartAngle=6e-16 EndAngle=3.14159
    g1: ArcOfCircle CenterX=-34.2 CenterY=-10.5 CenterZ=0 NormalX=0 NormalY=0 NormalZ=1 AngleXU=0 Radius=1.5 StartAngle=0 EndAngle=3.14159
    g2: ArcOfCircle CenterX=-34.2 CenterY=-27.7 CenterZ=0 NormalX=0 NormalY=0 NormalZ=1 AngleXU=0 Radius=1.5 StartAngle=3.14159 EndAngle=6.28319
    g3: ArcOfCircle CenterX=-4 CenterY=-27.7 CenterZ=0 NormalX=0 NormalY=0 NormalZ=1 AngleXU=0 Radius=1.5 StartAngle=3.1416 EndAngle=6.28319
    g4: ArcOfCircle CenterX=-10 CenterY=-4.3 CenterZ=0 NormalX=0 NormalY=0 NormalZ=1 AngleXU=0 Radius=1.5 StartAngle=2e-16 EndAngle=3.14159
    g5: ArcOfCircle CenterX=-16.1 CenterY=-1.8 CenterZ=0 NormalX=0 NormalY=0 NormalZ=1 AngleXU=0 Radius=1.5 StartAngle=5e-16 EndAngle=3.14159
    g6: ArcOfCircle CenterX=-22.1 CenterY=-1.8 CenterZ=0 NormalX=0 NormalY=0 NormalZ=1 AngleXU=0 Radius=1.5 StartAngle=5e-16 EndAngle=3.14159
    g7: ArcOfCircle CenterX=-28.2 CenterY=-4.3 CenterZ=0 NormalX=0 NormalY=0 NormalZ=1 AngleXU=0 Radius=1.5 StartAngle=2e-16 EndAngle=3.14159
    g8: ArcOfCircle CenterX=-10 CenterY=-33.9 CenterZ=0 NormalX=0 NormalY=0 NormalZ=1 AngleXU=0 Radius=1.5 StartAngle=3.14159 EndAngle=6.28319
    g9: ArcOfCircle CenterX=-16.1 CenterY=-36.4 CenterZ=0 NormalX=0 NormalY=0 NormalZ=1 AngleXU=0 Radius=1.5 StartAngle=3.14159 EndAngle=6.28319
    g10: ArcOfCircle CenterX=-22.1 CenterY=-36.4 CenterZ=0 NormalX=0 NormalY=0 NormalZ=1 AngleXU=0 Radius=1.5 StartAngle=3.14159 EndAngle=6.28319
    g11: ArcOfCircle CenterX=-28.2 CenterY=-33.9 CenterZ=0 NormalX=0 NormalY=0 NormalZ=1 AngleXU=0 Radius=1.5 StartAngle=3.14159 EndAngle=6.28319
    g12: LineSegment StartX=-35.7 StartY=-10.5 StartZ=0 EndX=-35.7 EndY=-27.7 EndZ=0
    g13: LineSegment StartX=-32.7 StartY=-10.5 StartZ=0 EndX=-32.7 EndY=-27.7 EndZ=0
    g14: LineSegment StartX=-29.7 StartY=-33.9 StartZ=0 EndX=-29.7 EndY=-4.3 EndZ=0
    g15: LineSegment StartX=-26.7 StartY=-33.9 StartZ=0 EndX=-26.7 EndY=-4.3 EndZ=0
    g16: LineSegment StartX=-2.5 StartY=-10.5 StartZ=0 EndX=-2.5 EndY=-27.7 EndZ=0
    g17: LineSegment StartX=-8.5 StartY=-4.3 StartZ=0 EndX=-8.5 EndY=-33.9 EndZ=0
    g18: LineSegment StartX=-5.5 StartY=-10.5 StartZ=0 EndX=-5.5 EndY=-27.7 EndZ=0
    g19: LineSegment StartX=-11.5 StartY=-4.3 StartZ=0 EndX=-11.5 EndY=-33.9 EndZ=0
    g20: LineSegment StartX=-14.6 StartY=-1.8 StartZ=0 EndX=-14.6 EndY=-36.4 EndZ=0
    g21: LineSegment StartX=-17.6 StartY=-1.8 StartZ=0 EndX=-17.6 EndY=-36.4 EndZ=0
    g22: LineSegment StartX=-20.6 StartY=-36.4 StartZ=0 EndX=-20.6 EndY=-1.8 EndZ=0
    g23: LineSegment StartX=-23.6 StartY=-1.8 StartZ=0 EndX=-23.6 EndY=-36.4 EndZ=0
  constraints (48):
    c: Block(g0)
    c: Block(g1)
    c: Block(g2)
    c: Block(g3)
    c: Block(g4)
    c: Block(g5)
    c: Block(g6)
    c: Block(g7)
    c: Block(g8)
    c: Block(g9)
    c: Block(g10)
    c: Block(g11)
    c: Coincident(g12,g1)
    c: Coincident(g12,g2)
    c: Vertical(g12)
    c: Coincident(g13,g1)
    c: Coincident(g13,g2)
    c: Vertical(g13)
    c: Coincident(g14,g11)
    c: Coincident(g14,g7)
    c: Vertical(g14)
    c: Coincident(g15,g11)
    c: Coincident(g15,g7)
    c: Vertical(g15)
    c: Coincident(g16,g0)
    c: Coincident(g16,g3)
    c: Vertical(g16)
    c: Coincident(g17,g4)
    c: Coincident(g17,g8)
    c: Vertical(g17)
    c: Coincident(g18,g0)
    c: Coincident(g18,g3)
    c: Vertical(g18)
    c: Coincident(g19,g4)
    c: Coincident(g19,g8)
    c: Vertical(g19)
    c: Coincident(g20,g5)
    c: Coincident(g20,g9)
    c: Vertical(g20)
    c: Coincident(g21,g5)
    c: Coincident(g21,g9)
    c: Vertical(g21)
    c: Coincident(g22,g10)
    c: Coincident(g22,g6)
    c: Vertical(g22)
    c: Coincident(g23,g6)
    c: Coincident(g23,g10)
    c: Vertical(g23)
FEATURE [Part::Extrusion] Extrude020  label="removeToCreateFanGrillHoles"
  Base = -> Sketch029
  Dir = (0,-1,6e-16)
  DirMode = 2
  FaceMakerClass = Part::FaceMakerBullseye
  LengthFwd = 10
  LengthRev = 0
  Placement = pos=(65.4,44,54.82) rot=(0,0,1;0rad)
  Solid = true
  Symmetric = false
FEATURE [Part::MultiFuse] Fusion055  label="top008"
  Shapes = -> [Cut017,Cut018]
FEATURE [Part::Cut] Cut019  label="top009"
  Base = -> Fusion055
  Tool = -> Extrude020
FEATURE [App::MeasureDistance] Distance003  label="Distance: 71.95 mm"
  Distance = 71.9513
  P1 = (117,38,72)
  P2 = (117,38,0.0487319)
FEATURE [Sketcher::SketchObject] Sketch030
  FullyConstrained = true
  Placement = pos=(0,0,0) rot=(0.57735,0.57735,0.57735;2.0944rad)
  sketch-geometry (1):
    g0: LineSegment StartX=0 StartY=0 StartZ=0 EndX=0 EndY=22 EndZ=0
  constraints (3):
    c: Coincident(g0,g-1)
    c: Distance(g0) = 22
    c: Vertical(g0)
